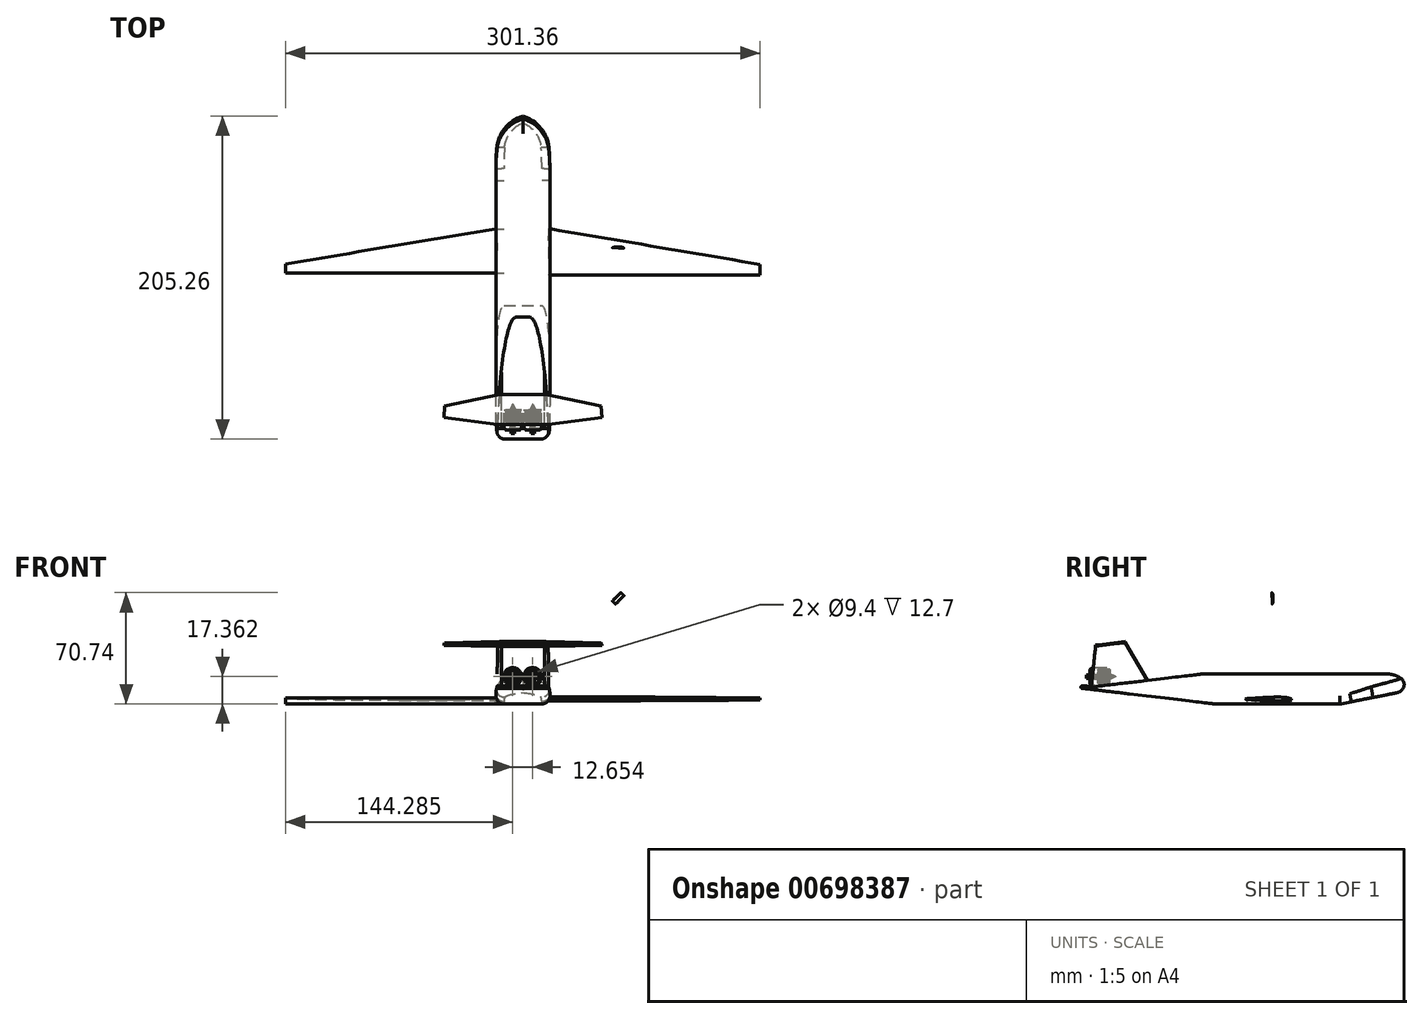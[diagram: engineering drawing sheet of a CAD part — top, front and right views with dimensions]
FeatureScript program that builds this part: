
annotation { "Feature Type Name" : "Feature", "Feature Type Description" : "" }
export const myFeature = defineFeature(function(context is Context, id is Id, definition is map)
    precondition{}
    {
        {
            var Q0;
            Q0=qCreatedBy(makeId("Top.planeOp"),FACE);
            var sketch = newSketch(context, id + "F0", { "sketchPlane" : qUnion([Q0])});
            skLineSegment(sketch, "E0.bottom", {"start": v(17.15, 104.78) * mm, "end": v(-17.14, 104.78) * mm});
            skLineSegment(sketch, "E0.top", {"start": v(17.14, -104.78) * mm, "end": v(-17.15, -104.78) * mm});
            skLineSegment(sketch, "E0.left", {"start": v(17.15, 104.78) * mm, "end": v(17.14, -104.78) * mm});
            skLineSegment(sketch, "E0.right", {"start": v(-17.14, 104.78) * mm, "end": v(-17.15, -104.78) * mm});
            skPoint(sketch, "E0.middle", {"position": v(0, 0) * mm});
            skSolve(sketch);
        }
        {
            var Q0;
            Q0=makeQuery(id+"F0.imprint","IMPRINT",FACE,{"disambiguationData":[TD([[makeQuery(id+"F0.imprint","IMPRINT",EDGE,{"derivedFrom":sQuery(id+"F0.wireOp",EDGE,"E0.bottom")}),1.0]])]});
            extrude(context, id + "F1", {"entities" : qUnion([Q0]), "depth" : 19.05 * mm, "offsetDistance" : 25.4 * mm});
        }
        {
            var Q0;
            Q0=makeQuery(id+"F1.opExtrude","SWEPT_EDGE",EDGE,{"disambiguationData":[OSD([sQuery(id+"F0.wireOp",EDGE,"E0.bottom"),sQuery(id+"F0.wireOp",EDGE,"E0.left")])]});
            var Q1;
            Q1=makeQuery(id+"F1.opExtrude","SWEPT_EDGE",EDGE,{"disambiguationData":[OSD([sQuery(id+"F0.wireOp",EDGE,"E0.bottom"),sQuery(id+"F0.wireOp",EDGE,"E0.right")])]});
            fillet(context, id + "F2", {"entities" : qUnion([Q0, Q1]), "radius" : 25.4 * mm, "tangentPropagation" : true, "allowEdgeOverflow" : false});
        }
        {
            var Q0;
            Q0=makeQuery(id+"F1.opExtrude","SWEPT_FACE",FACE,{"disambiguationData":[OSD([sQuery(id+"F0.wireOp",EDGE,"E0.right")])]});
            var sketch = newSketch(context, id + "F3", { "sketchPlane" : qUnion([Q0])});
            skLineSegment(sketch, "E1.bottom", {"start": v(-28.56, 19.05) * mm, "end": v(-0.6, 19.05) * mm});
            skLineSegment(sketch, "E1.top", {"start": v(-28.56, 0) * mm, "end": v(-0.6, 0) * mm});
            skLineSegment(sketch, "E1.left", {"start": v(-28.56, 19.05) * mm, "end": v(-28.56, 0) * mm});
            skLineSegment(sketch, "E1.right", {"start": v(-0.6, 19.05) * mm, "end": v(-0.6, 0) * mm});
            skLineSegment(sketch, "E2", {"start": v(-28.56, 6.35) * mm, "end": v(-0.6, 6.35) * mm});
            skFitSpline(sketch, "E3", {"points": [v(0.31, 4.07) * mm, v(-28.37, 4.63) * mm, v(-27.2, 2.97) * mm, v(-7.39, 2.92) * mm, v(-5.4, 3.55) * mm, v(0.31, 4.07) * mm]});
            skPoint(sketch, "E4", {"position": v(1.95, 0.65) * mm});
            skPoint(sketch, "E5", {"position": v(4.62, -0.4) * mm});
            skSolve(sketch);
        }
        {
            var Q0;
            Q0=makeQuery(id+"F1.opExtrude","SWEPT_FACE",FACE,{"disambiguationData":[OSD([sQuery(id+"F0.wireOp",EDGE,"E0.left")])]});
            var sketch = newSketch(context, id + "F4", { "sketchPlane" : qUnion([Q0])});
            skLineSegment(sketch, "E6.bottom", {"start": v(-0.54, 19.05) * mm, "end": v(28.71, 19.05) * mm});
            skLineSegment(sketch, "E6.top", {"start": v(-0.54, 0) * mm, "end": v(28.71, 0) * mm});
            skLineSegment(sketch, "E6.left", {"start": v(-0.54, 19.05) * mm, "end": v(-0.54, 0) * mm});
            skLineSegment(sketch, "E6.right", {"start": v(28.71, 19.05) * mm, "end": v(28.71, 0) * mm});
            skLineSegment(sketch, "E7", {"start": v(-0.54, 6.35) * mm, "end": v(28.71, 6.35) * mm});
            skSolve(sketch);
        }
        {
            var Q0;
            {var subQ0=sQuery(id+"F0.wireOp",EDGE,"E0.right");Q0=makeQuery(id+"FtCAVRDJn0QG3nM_1.boolean.opBoolean","SPLIT",EDGE,{"disambiguationData":[TD([makeQuery(id+"FtCAVRDJn0QG3nM_1.opExtrude","SWEPT_FACE",FACE,{"disambiguationData":[OSD([sQuery(id+"F3.wireOp",EDGE,"E1.right")])]})])],"derivedFrom":makeQuery(id+"F1.opExtrude","CAP_EDGE",EDGE,{"disambiguationData":[OSD([subQ0])],"isStart":false})});}
            var Q1;
            {var subQ0=sQuery(id+"F0.wireOp",EDGE,"E0.left");Q1=makeQuery(id+"FXmawxG26BbFG8q_1.boolean.opBoolean","SPLIT",EDGE,{"disambiguationData":[TD([makeQuery(id+"FXmawxG26BbFG8q_1.opExtrude","SWEPT_FACE",FACE,{"disambiguationData":[OSD([sQuery(id+"F4.wireOp",EDGE,"E6.right")])]})])],"derivedFrom":makeQuery(id+"F1.opExtrude","CAP_EDGE",EDGE,{"disambiguationData":[OSD([subQ0])],"isStart":false})});}
            var Q2;
            {var subQ0=sQuery(id+"F0.wireOp",EDGE,"E0.right");Q2=makeQuery(id+"FtCAVRDJn0QG3nM_1.boolean.opBoolean","SPLIT",EDGE,{"disambiguationData":[TD([makeQuery(id+"FtCAVRDJn0QG3nM_1.opExtrude","SWEPT_FACE",FACE,{"disambiguationData":[OSD([sQuery(id+"F3.wireOp",EDGE,"E1.left")])]})])],"derivedFrom":makeQuery(id+"F1.opExtrude","CAP_EDGE",EDGE,{"disambiguationData":[OSD([subQ0])],"isStart":false})});}
            fillet(context, id + "F5", {"entities" : qUnion([Q0, Q1, Q2]), "radius" : 12.7 * mm, "tangentPropagation" : true, "allowEdgeOverflow" : false});
        }
        {
            var Q0;
            {var subQ0=sQuery(id+"F0.wireOp",EDGE,"E0.left");Q0=makeQuery(id+"FXmawxG26BbFG8q_1.boolean.opBoolean","SPLIT",EDGE,{"disambiguationData":[TD([makeQuery(id+"FXmawxG26BbFG8q_1.opExtrude","SWEPT_FACE",FACE,{"disambiguationData":[OSD([sQuery(id+"F4.wireOp",EDGE,"E6.left")])]})])],"derivedFrom":makeQuery(id+"F1.opExtrude","CAP_EDGE",EDGE,{"disambiguationData":[OSD([subQ0])],"isStart":true})});}
            var Q1;
            {var subQ0=sQuery(id+"F0.wireOp",EDGE,"E0.left");Q1=makeQuery(id+"FXmawxG26BbFG8q_1.boolean.opBoolean","SPLIT",EDGE,{"disambiguationData":[TD([makeQuery(id+"FXmawxG26BbFG8q_1.opExtrude","SWEPT_FACE",FACE,{"disambiguationData":[OSD([sQuery(id+"F4.wireOp",EDGE,"E6.right")])]})])],"derivedFrom":makeQuery(id+"F1.opExtrude","CAP_EDGE",EDGE,{"disambiguationData":[OSD([subQ0])],"isStart":true})});}
            var Q2;
            {var subQ0=sQuery(id+"F0.wireOp",EDGE,"E0.right");Q2=makeQuery(id+"FtCAVRDJn0QG3nM_1.boolean.opBoolean","SPLIT",EDGE,{"disambiguationData":[TD([makeQuery(id+"FtCAVRDJn0QG3nM_1.opExtrude","SWEPT_FACE",FACE,{"disambiguationData":[OSD([sQuery(id+"F3.wireOp",EDGE,"E1.left")])]})])],"derivedFrom":makeQuery(id+"F1.opExtrude","CAP_EDGE",EDGE,{"disambiguationData":[OSD([subQ0])],"isStart":true})});}
            fillet(context, id + "F6", {"entities" : qUnion([Q0, Q1, Q2]), "radius" : 5.08 * mm, "tangentPropagation" : true, "allowEdgeOverflow" : false});
        }
        {
            var Q0;
            {var subQ0=sQuery(id+"F4.wireOp",EDGE,"E6.top");Q0=makeQuery(id+"F4.imprint","IMPRINT",FACE,{"disambiguationData":[TD([[makeQuery(id+"F4.imprint","IMPRINT",EDGE,{"derivedFrom":subQ0}),-1.0]])]});}
            var sketch = newSketch(context, id + "F7", { "sketchPlane" : qUnion([Q0])});
            skFitSpline(sketch, "E8", {"points": [v(-0.34, 3.05) * mm, v(29.07, 2.53) * mm, v(26.42, 3.88) * mm, v(4.03, 3.53) * mm, v(-0.34, 3.05) * mm]});
            skPoint(sketch, "E9", {"position": v(24.34, 2.06) * mm});
            skPoint(sketch, "E10", {"position": v(2.71, 2.74) * mm});
            skPoint(sketch, "E11", {"position": v(2.15, 3.42) * mm});
            skPoint(sketch, "E12", {"position": v(1.26, 2.86) * mm});
            skSolve(sketch);
        }
        {
            var Q0;
            Q0=makeQuery(id+"F7.imprint","IMPRINT",FACE,{"disambiguationData":[TD([[makeQuery(id+"F7.imprint","IMPRINT",EDGE,{"derivedFrom":sQuery(id+"F7.wireOp",EDGE,"E8")}),1.0]])]});
            extrude(context, id + "F8", {"entities" : qUnion([Q0]), "operationType" : NewBodyOperationType.ADD, "depth" : 133.54 * mm, "offsetDistance" : 25.4 * mm, "hasSecondDirection" : true, "secondDirectionOppositeDirection" : true, "secondDirectionDepth" : 25.4 * mm});
        }
        {
            var Q0;
            {var subQ0=sQuery(id+"F3.wireOp",EDGE,"E3");var subQ1=sQuery(id+"F3.wireOp",EDGE,"E1.left");var subQ2=makeQuery(id+"F3.imprint","INTERSECT",VERTEX,{"disambiguationData":[OD(0.0)],"derivedFrom":[subQ1,subQ0]});Q0=makeQuery(id+"F3.imprint","IMPRINT",FACE,{"disambiguationData":[TD([[makeQuery(id+"F3.imprint","IMPRINT",EDGE,{"disambiguationData":[TD([[subQ2,-1.0]])],"derivedFrom":subQ1}),1.0]])]});}
            extrude(context, id + "F9", {"entities" : qUnion([Q0]), "operationType" : NewBodyOperationType.ADD, "depth" : 133.54 * mm, "offsetDistance" : 25.4 * mm, "hasSecondDirection" : true, "secondDirectionOppositeDirection" : true, "secondDirectionDepth" : 25.4 * mm});
        }
        {
            var Q0;
            Q0=qCreatedBy(makeId("Right.planeOp"),FACE);
            var sketch = newSketch(context, id + "F10", { "sketchPlane" : qUnion([Q0])});
            skLineSegment(sketch, "E13.bottom", {"start": v(19.48, 67.25) * mm, "end": v(46.84, 67.25) * mm});
            skLineSegment(sketch, "E13.top", {"start": v(19.48, 55.36) * mm, "end": v(46.84, 55.36) * mm});
            skLineSegment(sketch, "E13.left", {"start": v(19.48, 67.25) * mm, "end": v(19.48, 55.36) * mm});
            skLineSegment(sketch, "E13.right", {"start": v(46.84, 67.25) * mm, "end": v(46.84, 55.36) * mm});
            skSolve(sketch);
        }
        {
            var Q0;
            Q0=makeQuery(id+"F10.imprint","IMPRINT",FACE,{"disambiguationData":[TD([[makeQuery(id+"F10.imprint","IMPRINT",EDGE,{"derivedFrom":sQuery(id+"F10.wireOp",EDGE,"E13.bottom")}),-1.0]])]});
            extrude(context, id + "F11", {"entities" : qUnion([Q0]), "depth" : 81.28 * mm, "offsetDistance" : 25.4 * mm});
        }
        {
            var Q0;
            Q0=makeQuery(id+"F11.opExtrude","SWEPT_FACE",FACE,{"disambiguationData":[OSD([sQuery(id+"F10.wireOp",EDGE,"E13.bottom")])]});
            var sketch = newSketch(context, id + "F12", { "sketchPlane" : qUnion([Q0])});
            skLineSegment(sketch, "E14", {"start": v(0, 46.84) * mm, "end": v(81.28, 27.08) * mm});
            skSolve(sketch);
        }
        {
            var Q0;
            {var subQ0=sQuery(id+"F12.wireOp",EDGE,"E14");Q0=makeQuery(id+"F12.imprint","IMPRINT",FACE,{"disambiguationData":[TD([[makeQuery(id+"F12.imprint","IMPRINT",EDGE,{"derivedFrom":subQ0}),1.0]])]});}
            extrude(context, id + "F13", {"entities" : qUnion([Q0]), "operationType" : NewBodyOperationType.REMOVE, "oppositeDirection" : true, "depth" : 25.4 * mm, "offsetDistance" : 25.4 * mm});
        }
        {
            var Q0;
            Q0=makeQuery(id+"F11.opExtrude","SWEPT_BODY",BODY,{"disambiguationData":[OSD([sQuery(id+"F10.wireOp",EDGE,"E13.bottom"),sQuery(id+"F10.wireOp",EDGE,"E13.top"),sQuery(id+"F10.wireOp",EDGE,"E13.left"),sQuery(id+"F10.wireOp",EDGE,"E13.right")])]});
            deleteBodies(context, id + "F14", {"entities" : qUnion([Q0])});
        }
        {
            var Q0;
            {var subQ0=sQuery(id+"F4.wireOp",EDGE,"E6.top");Q0=makeQuery(id+"F4.imprint","IMPRINT",FACE,{"disambiguationData":[TD([[makeQuery(id+"F4.imprint","IMPRINT",EDGE,{"derivedFrom":subQ0}),-1.0]])]});}
            var sketch = newSketch(context, id + "F15", { "sketchPlane" : qUnion([Q0])});
            skLineSegment(sketch, "E15.bottom", {"start": v(0, 5.25) * mm, "end": v(28.83, 5.25) * mm});
            skLineSegment(sketch, "E15.top", {"start": v(0, 4.61) * mm, "end": v(28.83, 4.61) * mm});
            skLineSegment(sketch, "E15.left", {"start": v(0, 5.25) * mm, "end": v(0, 4.61) * mm});
            skLineSegment(sketch, "E15.right", {"start": v(28.83, 5.25) * mm, "end": v(28.83, 4.61) * mm});
            skSolve(sketch);
        }
        {
            var Q0;
            {var subQ0=sQuery(id+"F15.wireOp",EDGE,"E15.left");Q0=makeQuery(id+"F15.imprint","IMPRINT",FACE,{"disambiguationData":[TD([[makeQuery(id+"F15.imprint","IMPRINT",EDGE,{"derivedFrom":subQ0}),1.0]])]});}
            extrude(context, id + "F16", {"entities" : qUnion([Q0]), "operationType" : NewBodyOperationType.ADD, "depth" : 133.54 * mm, "offsetDistance" : 25.4 * mm});
        }
        {
            var Q0;
            Q0=makeQuery(id+"F16.opExtrude","SWEPT_FACE",FACE,{"disambiguationData":[OSD([sQuery(id+"F15.wireOp",EDGE,"E15.bottom")])]});
            var sketch = newSketch(context, id + "F17", { "sketchPlane" : qUnion([Q0])});
            skLineSegment(sketch, "E16", {"start": v(17.15, 28.71) * mm, "end": v(150.68, 6.07) * mm});
            skSolve(sketch);
        }
        {
            var Q0;
            {var subQ0=sQuery(id+"F17.wireOp",EDGE,"E16");Q0=makeQuery(id+"F17.imprint","IMPRINT",FACE,{"disambiguationData":[TD([[makeQuery(id+"F17.imprint","IMPRINT",EDGE,{"derivedFrom":subQ0}),1.0]])]});}
            extrude(context, id + "F18", {"entities" : qUnion([Q0]), "operationType" : NewBodyOperationType.REMOVE, "oppositeDirection" : true, "depth" : 25.4 * mm, "offsetDistance" : 25.4 * mm});
        }
        {
            var Q0;
            Q0=makeQuery(id+"F16.opExtrude","SWEPT_FACE",FACE,{"disambiguationData":[OSD([sQuery(id+"F15.wireOp",EDGE,"E15.bottom")])]});
            var sketch = newSketch(context, id + "F19", { "sketchPlane" : qUnion([Q0])});
            skLineSegment(sketch, "E17", {"start": v(17.15, 28.71) * mm, "end": v(150.68, 6.07) * mm});
            skLineSegment(sketch, "E18", {"start": v(150.68, 6.07) * mm, "end": v(150.68, 0) * mm});
            skLineSegment(sketch, "E19", {"start": v(150.68, 0) * mm, "end": v(17.14, 0) * mm});
            skLineSegment(sketch, "E20", {"start": v(17.14, 0) * mm, "end": v(17.15, 28.71) * mm});
            skSolve(sketch);
        }
        {
            var Q0;
            Q0=makeQuery(id+"F19.imprint","IMPRINT",FACE,{"disambiguationData":[TD([[makeQuery(id+"F19.imprint","IMPRINT",EDGE,{"derivedFrom":sQuery(id+"F19.wireOp",EDGE,"E17")}),-1.0]])]});
            extrude(context, id + "F20", {"entities" : qUnion([Q0]), "operationType" : NewBodyOperationType.REMOVE, "endBound" : BoundingType.UP_TO_NEXT, "oppositeDirection" : true, "depth" : 2.54 * mm, "offsetDistance" : 25.4 * mm});
        }
        {
            var Q0;
            Q0=makeQuery(id+"F1.opExtrude","SWEPT_FACE",FACE,{"disambiguationData":[OSD([sQuery(id+"F0.wireOp",EDGE,"E0.right")])]});
            var sketch = newSketch(context, id + "F21", { "sketchPlane" : qUnion([Q0])});
            skLineSegment(sketch, "E21.bottom", {"start": v(-28.66, 6.35) * mm, "end": v(-0.3, 6.35) * mm});
            skLineSegment(sketch, "E21.top", {"start": v(-28.66, 5.62) * mm, "end": v(-0.3, 5.62) * mm});
            skLineSegment(sketch, "E21.left", {"start": v(-28.66, 6.35) * mm, "end": v(-28.66, 5.62) * mm});
            skLineSegment(sketch, "E21.right", {"start": v(-0.3, 6.35) * mm, "end": v(-0.3, 5.62) * mm});
            skSolve(sketch);
        }
        {
            var Q0;
            Q0=makeQuery(id+"F21.imprint","IMPRINT",FACE,{"disambiguationData":[TD([[makeQuery(id+"F21.imprint","IMPRINT",EDGE,{"derivedFrom":sQuery(id+"F21.wireOp",EDGE,"E21.bottom")}),1.0]])]});
            extrude(context, id + "F22", {"entities" : qUnion([Q0]), "operationType" : NewBodyOperationType.ADD, "depth" : 133.54 * mm, "offsetDistance" : 25.4 * mm});
        }
        {
            var Q0;
            Q0=makeQuery(id+"F22.opExtrude","SWEPT_FACE",FACE,{"disambiguationData":[OSD([sQuery(id+"F21.wireOp",EDGE,"E21.bottom")])]});
            var sketch = newSketch(context, id + "F23", { "sketchPlane" : qUnion([Q0])});
            skLineSegment(sketch, "E22", {"start": v(-17.14, 28.66) * mm, "end": v(-150.68, 6.36) * mm});
            skSolve(sketch);
        }
        {
            var Q0;
            {var subQ0=sQuery(id+"F23.wireOp",EDGE,"E22");Q0=makeQuery(id+"F23.imprint","IMPRINT",FACE,{"disambiguationData":[TD([[makeQuery(id+"F23.imprint","IMPRINT",EDGE,{"derivedFrom":subQ0}),-1.0]])]});}
            extrude(context, id + "F24", {"entities" : qUnion([Q0]), "operationType" : NewBodyOperationType.REMOVE, "oppositeDirection" : true, "depth" : 25.4 * mm, "offsetDistance" : 25.4 * mm});
        }
        {
            var Q0;
            Q0=makeQuery(id+"F22.opExtrude","SWEPT_FACE",FACE,{"disambiguationData":[OSD([sQuery(id+"F21.wireOp",EDGE,"E21.bottom")])]});
            extrude(context, id + "F25", {"entities" : qUnion([Q0]), "operationType" : NewBodyOperationType.REMOVE, "endBound" : BoundingType.UP_TO_NEXT, "oppositeDirection" : true, "depth" : 25.4 * mm, "offsetDistance" : 25.4 * mm});
        }
        {
            var Q0;
            Q0=makeQuery(id+"F5.opFillet","BLEND_EDGE",EDGE,{"blendedFrom":[makeQuery(id+"F1.opExtrude","CAP_EDGE",EDGE,{"disambiguationData":[OSD([sQuery(id+"F0.wireOp",EDGE,"E0.left")])],"isStart":false}),makeQuery(id+"F1.opExtrude","SWEPT_FACE",FACE,{"disambiguationData":[OSD([sQuery(id+"F0.wireOp",EDGE,"E0.top")])]})],"blendedInto":[makeQuery(id+"F1.opExtrude","SWEPT_FACE",FACE,{"disambiguationData":[OSD([sQuery(id+"F0.wireOp",EDGE,"E0.top")])]})]});
            fillet(context, id + "F26", {"entities" : qUnion([Q0]), "radius" : 5.08 * mm, "tangentPropagation" : true, "allowEdgeOverflow" : false});
        }
        {
            var Q0;
            {var subQ0=sQuery(id+"F0.wireOp",EDGE,"E0.left");var subQ2=makeQuery(id+"F1.opExtrude","SWEPT_EDGE",EDGE,{"disambiguationData":[OSD([sQuery(id+"F0.wireOp",EDGE,"E0.top"),subQ0])]});Q0=makeQuery(id+"F4.imprint","IMPRINT",FACE,{"disambiguationData":[TD([[makeQuery(id+"F4.imprint","IMPRINT",EDGE,{"derivedFrom":subQ2}),1.0]])]});}
            var sketch = newSketch(context, id + "F27", { "sketchPlane" : qUnion([Q0])});
            skLineSegment(sketch, "E23", {"start": v(-12.6, 20.8) * mm, "end": v(-104.7, 9.97) * mm});
            skLineSegment(sketch, "E24", {"start": v(-104.7, 9.97) * mm, "end": v(-20.12, 0) * mm});
            skLineSegment(sketch, "E25", {"start": v(-12.6, 20.8) * mm, "end": v(-20.12, 0) * mm});
            skSolve(sketch);
        }
        {
            var Q0;
            {var subQ6=sQuery(id+"F27.wireOp",EDGE,"E24");Q0=makeQuery(id+"F27.imprint","IMPRINT",FACE,{"disambiguationData":[TD([[makeQuery(id+"F27.imprint","IMPRINT",EDGE,{"derivedFrom":subQ6}),-1.0]])]});}
            extrude(context, id + "F28", {"entities" : qUnion([Q0]), "operationType" : NewBodyOperationType.REMOVE, "endBound" : BoundingType.THROUGH_ALL, "oppositeDirection" : true, "depth" : 25.4 * mm, "offsetDistance" : 25.4 * mm});
        }
        {
            var Q0;
            Q0=makeQuery(id+"F28.boolean.opBoolean","COPY",FACE,{"derivedFrom":makeQuery(id+"F28.opExtrude","SWEPT_FACE",FACE,{"disambiguationData":[OSD([sQuery(id+"F27.wireOp",EDGE,"E23")])]})});
            var sketch = newSketch(context, id + "F29", { "sketchPlane" : qUnion([Q0])});
            skLineSegment(sketch, "E26", {"start": v(-12.1, -102.82) * mm, "end": v(12.1, -102.82) * mm});
            skLineSegment(sketch, "E27", {"start": v(12.1, -102.82) * mm, "end": v(12.1, -96.37) * mm});
            skLineSegment(sketch, "E28", {"start": v(12.1, -96.37) * mm, "end": v(-12.1, -96.37) * mm});
            skLineSegment(sketch, "E29", {"start": v(-12.1, -96.37) * mm, "end": v(-12.1, -102.82) * mm});
            skLineSegment(sketch, "E30", {"start": v(12.1, -96.37) * mm, "end": v(16.37, -96.37) * mm});
            skLineSegment(sketch, "E31", {"start": v(16.37, -96.37) * mm, "end": v(16.43, -97.78) * mm});
            skLineSegment(sketch, "E32", {"start": v(16.43, -97.78) * mm, "end": v(12.1, -102.82) * mm});
            skLineSegment(sketch, "E33", {"start": v(-12.1, -102.82) * mm, "end": v(-16.43, -97.78) * mm});
            skLineSegment(sketch, "E34", {"start": v(-12.1, -96.37) * mm, "end": v(-16.37, -96.37) * mm});
            skSolve(sketch);
        }
        {
            var Q0;
            Q0=makeQuery(id+"F29.imprint","IMPRINT",FACE,{"disambiguationData":[TD([[makeQuery(id+"F29.imprint","IMPRINT",EDGE,{"derivedFrom":sQuery(id+"F29.wireOp",EDGE,"E26")}),1.0]])]});
            var Q1;
            Q1=makeQuery(id+"F29.imprint","IMPRINT",FACE,{"disambiguationData":[TD([[makeQuery(id+"F29.imprint","IMPRINT",EDGE,{"derivedFrom":sQuery(id+"F29.wireOp",EDGE,"E27")}),-1.0]])]});
            var Q2;
            Q2=makeQuery(id+"F29.imprint","IMPRINT",FACE,{"disambiguationData":[TD([[makeQuery(id+"F29.imprint","IMPRINT",EDGE,{"derivedFrom":sQuery(id+"F29.wireOp",EDGE,"E29")}),-1.0]])]});
            var Q3;
            Q3=makeQuery(id+"F29.imprint","IMPRINT",FACE,{"disambiguationData":[TD([[makeQuery(id+"F29.imprint","IMPRINT",EDGE,{"derivedFrom":sQuery(id+"F29.wireOp",EDGE,"E32")}),1.0]])]});
            var Q4;
            Q4=makeQuery(id+"F29.imprint","IMPRINT",FACE,{"disambiguationData":[TD([[makeQuery(id+"F29.imprint","IMPRINT",EDGE,{"derivedFrom":sQuery(id+"F29.wireOp",EDGE,"E33")}),1.0]])]});
            extrude(context, id + "F30", {"entities" : qUnion([Q0, Q1, Q2, Q3, Q4]), "operationType" : NewBodyOperationType.ADD, "depth" : 1.27 * mm, "offsetDistance" : 25.4 * mm});
        }
        {
            var Q0;
            Q0=makeQuery(id+"F30.opExtrude","CAP_EDGE",EDGE,{"disambiguationData":[OSD([sQuery(id+"F29.wireOp",EDGE,"E28"),sQuery(id+"F29.wireOp",EDGE,"E30"),sQuery(id+"F29.wireOp",EDGE,"E34")])],"isStart":false});
            fillet(context, id + "F31", {"entities" : qUnion([Q0]), "radius" : 15.94 * mm, "tangentPropagation" : true, "allowEdgeOverflow" : false});
        }
        {
            var Q0;
            Q0=qCreatedBy(makeId("Right.planeOp"),FACE);
            var sketch = newSketch(context, id + "F32", { "sketchPlane" : qUnion([Q0])});
            skLineSegment(sketch, "E35", {"start": v(103.83, 8.7) * mm, "end": v(59.96, 0) * mm});
            skLineSegment(sketch, "E36", {"start": v(103.83, 8.7) * mm, "end": v(106.15, -3) * mm});
            skLineSegment(sketch, "E37", {"start": v(106.15, -3) * mm, "end": v(61.39, -8.19) * mm});
            skLineSegment(sketch, "E38", {"start": v(61.39, -8.19) * mm, "end": v(59.96, 0) * mm});
            skSolve(sketch);
        }
        {
            var Q0;
            Q0=makeQuery(id+"F32.imprint","IMPRINT",FACE,{"disambiguationData":[TD([[makeQuery(id+"F32.imprint","IMPRINT",EDGE,{"derivedFrom":sQuery(id+"F32.wireOp",EDGE,"E35")}),1.0]])]});
            extrude(context, id + "F33", {"entities" : qUnion([Q0]), "operationType" : NewBodyOperationType.REMOVE, "endBound" : BoundingType.SYMMETRIC, "oppositeDirection" : true, "depth" : 77.22 * mm, "offsetDistance" : 25.4 * mm});
        }
        {
            var Q0;
            {var subQ0=sQuery(id+"F0.wireOp",EDGE,"E0.right");var subQ1=sQuery(id+"F0.wireOp",EDGE,"E0.left");var subQ2=sQuery(id+"F0.wireOp",EDGE,"E0.top");var subQ3=sQuery(id+"F0.wireOp",EDGE,"E0.bottom");Q0=makeQuery(id+"F33.boolean.opBoolean","INTERSECT",EDGE,{"derivedFrom":[makeQuery(id+"F6.opFillet","BLEND_FACE",FACE,{"disambiguationData":[OSD([subQ3,subQ2,subQ1,subQ0]),TDD([makeQuery(id+"F2.opFillet","BLEND_EDGE",EDGE,{"blendedFrom":[makeQuery(id+"F1.opExtrude","SWEPT_EDGE",EDGE,{"disambiguationData":[OSD([subQ3,subQ0])]}),makeQuery(id+"F1.opExtrude","CAP_FACE",FACE,{"disambiguationData":[OSD([subQ3,subQ2,subQ1,subQ0])],"isStart":true})],"blendedInto":[makeQuery(id+"F1.opExtrude","CAP_FACE",FACE,{"disambiguationData":[OSD([subQ3,subQ2,subQ1,subQ0])],"isStart":true})]})])]}),makeQuery(id+"F33.opExtrude","SWEPT_FACE",FACE,{"disambiguationData":[OSD([sQuery(id+"F32.wireOp",EDGE,"E35")])]})]});}
            var Q1;
            Q1=makeQuery(id+"F33.boolean.opBoolean","INTERSECT",EDGE,{"derivedFrom":[makeQuery(id+"F6.opFillet","BLEND_FACE",FACE,{"disambiguationData":[OSD([sQuery(id+"F0.wireOp",EDGE,"E0.right")])]}),makeQuery(id+"F33.opExtrude","SWEPT_FACE",FACE,{"disambiguationData":[OSD([sQuery(id+"F32.wireOp",EDGE,"E35")])]})]});
            var Q2;
            Q2=makeQuery(id+"F33.boolean.opBoolean","COPY",FACE,{"derivedFrom":makeQuery(id+"F33.opExtrude","SWEPT_FACE",FACE,{"disambiguationData":[OSD([sQuery(id+"F32.wireOp",EDGE,"E35")])]})});
            fillet(context, id + "F34", {"entities" : qUnion([Q0, Q1, Q2]), "radius" : 5.08 * mm, "tangentPropagation" : true, "allowEdgeOverflow" : false});
        }
        {
            var Q0;
            Q0=makeQuery(id+"F28.boolean.opBoolean","COPY",FACE,{"derivedFrom":makeQuery(id+"F28.opExtrude","SWEPT_FACE",FACE,{"disambiguationData":[OSD([sQuery(id+"F27.wireOp",EDGE,"E23")])]})});
            var sketch = newSketch(context, id + "F35", { "sketchPlane" : qUnion([Q0])});
            skLineSegment(sketch, "E39.bottom", {"start": v(-16.37, -96.37) * mm, "end": v(-13.63, -96.37) * mm});
            skLineSegment(sketch, "E39.top", {"start": v(-16.37, -60.4) * mm, "end": v(-13.63, -60.4) * mm});
            skLineSegment(sketch, "E39.left", {"start": v(-16.37, -96.37) * mm, "end": v(-16.37, -60.4) * mm});
            skLineSegment(sketch, "E39.right", {"start": v(-13.63, -96.37) * mm, "end": v(-13.63, -60.4) * mm});
            skLineSegment(sketch, "E40.bottom", {"start": v(16.37, -96.37) * mm, "end": v(13.81, -96.37) * mm});
            skLineSegment(sketch, "E40.top", {"start": v(16.37, -60.4) * mm, "end": v(13.81, -60.4) * mm});
            skLineSegment(sketch, "E40.left", {"start": v(16.37, -96.37) * mm, "end": v(16.37, -60.4) * mm});
            skLineSegment(sketch, "E40.right", {"start": v(13.81, -96.37) * mm, "end": v(13.81, -60.4) * mm});
            skSolve(sketch);
        }
        {
            var Q0;
            {var subQ0=sQuery(id+"F35.wireOp",EDGE,"E39.bottom");Q0=makeQuery(id+"F35.imprint","IMPRINT",FACE,{"disambiguationData":[TD([[makeQuery(id+"F35.imprint","IMPRINT",EDGE,{"derivedFrom":subQ0}),-1.0]])]});}
            var Q1;
            {var subQ0=sQuery(id+"F35.wireOp",EDGE,"E40.bottom");Q1=makeQuery(id+"F35.imprint","IMPRINT",FACE,{"disambiguationData":[TD([[makeQuery(id+"F35.imprint","IMPRINT",EDGE,{"derivedFrom":subQ0}),-1.0]])]});}
            extrude(context, id + "F36", {"entities" : qUnion([Q0, Q1]), "operationType" : NewBodyOperationType.ADD, "depth" : 25.4 * mm, "offsetDistance" : 25.4 * mm});
        }
        {
            var Q0;
            Q0=makeQuery(id+"F36.opExtrude","SWEPT_FACE",FACE,{"disambiguationData":[OSD([sQuery(id+"F35.wireOp",EDGE,"E39.right")])]});
            var sketch = newSketch(context, id + "F37", { "sketchPlane" : qUnion([Q0])});
            skLineSegment(sketch, "E41", {"start": v(-98.3, 10.73) * mm, "end": v(-95.57, 36.62) * mm});
            skLineSegment(sketch, "E42", {"start": v(-76.52, 38.86) * mm, "end": v(-62.57, 14.93) * mm});
            skSolve(sketch);
        }
        {
            var Q0;
            {var subQ0=sQuery(id+"F37.wireOp",EDGE,"qg9zDmBJ-7vhe-sEv8-FbPa-SV9eqWlspidy");Q0=makeQuery(id+"F37.imprint","IMPRINT",FACE,{"disambiguationData":[TD([[makeQuery(id+"F37.imprint","IMPRINT",EDGE,{"derivedFrom":subQ0}),1.0]])]});}
            var Q1;
            {var subQ0=sQuery(id+"F37.wireOp",EDGE,"E41");Q1=makeQuery(id+"F37.imprint","IMPRINT",FACE,{"disambiguationData":[TD([[makeQuery(id+"F37.imprint","IMPRINT",EDGE,{"derivedFrom":subQ0}),1.0]])]});}
            var Q2;
            {var subQ0=sQuery(id+"F37.wireOp",EDGE,"E42");Q2=makeQuery(id+"F37.imprint","IMPRINT",FACE,{"disambiguationData":[TD([[makeQuery(id+"F37.imprint","IMPRINT",EDGE,{"derivedFrom":subQ0}),1.0]])]});}
            extrude(context, id + "F38", {"entities" : qUnion([Q0, Q1, Q2]), "operationType" : NewBodyOperationType.REMOVE, "oppositeDirection" : true, "depth" : 25.4 * mm, "offsetDistance" : 25.4 * mm});
        }
        {
            var Q0;
            Q0=makeQuery(id+"F36.opExtrude","SWEPT_FACE",FACE,{"disambiguationData":[OSD([sQuery(id+"F35.wireOp",EDGE,"E40.right")])]});
            var sketch = newSketch(context, id + "F39", { "sketchPlane" : qUnion([Q0])});
            skLineSegment(sketch, "E43", {"start": v(98.3, 10.73) * mm, "end": v(95.57, 36.62) * mm});
            skLineSegment(sketch, "E44", {"start": v(62.57, 14.93) * mm, "end": v(76.52, 38.86) * mm});
            skSolve(sketch);
        }
        {
            var Q0;
            {var subQ0=sQuery(id+"F39.wireOp",EDGE,"E44");Q0=makeQuery(id+"F39.imprint","IMPRINT",FACE,{"disambiguationData":[TD([[makeQuery(id+"F39.imprint","IMPRINT",EDGE,{"derivedFrom":subQ0}),1.0]])]});}
            var Q1;
            {var subQ0=sQuery(id+"F39.wireOp",EDGE,"E43");Q1=makeQuery(id+"F39.imprint","IMPRINT",FACE,{"disambiguationData":[TD([[makeQuery(id+"F39.imprint","IMPRINT",EDGE,{"derivedFrom":subQ0}),-1.0]])]});}
            extrude(context, id + "F40", {"entities" : qUnion([Q0, Q1]), "operationType" : NewBodyOperationType.REMOVE, "oppositeDirection" : true, "depth" : 25.4 * mm, "offsetDistance" : 25.4 * mm});
        }
        {
            var Q0;
            Q0=makeQuery(id+"F36.opExtrude","CAP_FACE",FACE,{"disambiguationData":[OSD([sQuery(id+"F0.wireOp",EDGE,"E0.right"),sQuery(id+"F27.wireOp",EDGE,"E23"),sQuery(id+"F35.wireOp",EDGE,"E39.bottom"),sQuery(id+"F35.wireOp",EDGE,"E39.top"),sQuery(id+"F35.wireOp",EDGE,"E39.right")])],"isStart":false});
            var sketch = newSketch(context, id + "F41", { "sketchPlane" : qUnion([Q0])});
            skLineSegment(sketch, "E45.bottom", {"start": v(-16.1, -90.64) * mm, "end": v(16.04, -90.64) * mm});
            skLineSegment(sketch, "E45.left", {"start": v(-16.1, -90.64) * mm, "end": v(-16.1, -71.7) * mm});
            skLineSegment(sketch, "E46", {"start": v(16.04, -90.64) * mm, "end": v(-16.1, -90.64) * mm});
            skLineSegment(sketch, "E47", {"start": v(-16.1, -90.64) * mm, "end": v(-14.85, -71.46) * mm});
            skLineSegment(sketch, "E48", {"start": v(-14.85, -71.46) * mm, "end": v(-13.63, -71.46) * mm});
            skLineSegment(sketch, "E49", {"start": v(-13.63, -71.46) * mm, "end": v(13.82, -71.46) * mm});
            skLineSegment(sketch, "E50", {"start": v(13.82, -71.46) * mm, "end": v(14.83, -71.46) * mm});
            skLineSegment(sketch, "E51", {"start": v(14.83, -71.46) * mm, "end": v(16.04, -90.64) * mm});
            skSolve(sketch);
        }
        {
            var Q0;
            Q0=makeQuery(id+"F41.imprint","IMPRINT",FACE,{"disambiguationData":[TD([[makeQuery(id+"F41.imprint","IMPRINT",EDGE,{"derivedFrom":sQuery(id+"F41.wireOp",EDGE,"E49")}),-1.0]])]});
            var Q1;
            {var subQ2=sQuery(id+"F41.wireOp",EDGE,"E47");Q1=makeQuery(id+"F41.imprint","IMPRINT",FACE,{"disambiguationData":[TD([[makeQuery(id+"F41.imprint","IMPRINT",EDGE,{"derivedFrom":subQ2}),-1.0]])]});}
            extrude(context, id + "F42", {"entities" : qUnion([Q0, Q1]), "operationType" : NewBodyOperationType.ADD, "depth" : 0.76 * mm, "offsetDistance" : 25.4 * mm});
        }
        {
            var Q0;
            Q0=makeQuery(id+"F42.opExtrude","SWEPT_FACE",FACE,{"disambiguationData":[OSD([sQuery(id+"F41.wireOp",EDGE,"E47")])]});
            extrude(context, id + "F43", {"entities" : qUnion([Q0]), "operationType" : NewBodyOperationType.ADD, "depth" : 34.3 * mm, "offsetDistance" : 25.4 * mm});
        }
        {
            var Q0;
            Q0=makeQuery(id+"F42.opExtrude","SWEPT_FACE",FACE,{"disambiguationData":[OSD([sQuery(id+"F41.wireOp",EDGE,"E51")])]});
            var sketch = newSketch(context, id + "F44", { "sketchPlane" : qUnion([Q0])});
            skLineSegment(sketch, "E52", {"start": v(-96.4, 36.5) * mm, "end": v(-96.5, 37.26) * mm});
            skLineSegment(sketch, "E53", {"start": v(-96.5, 37.26) * mm, "end": v(-77.4, 39.5) * mm});
            skLineSegment(sketch, "E54", {"start": v(-77.4, 39.5) * mm, "end": v(-77.32, 38.75) * mm});
            skLineSegment(sketch, "E55", {"start": v(-77.32, 38.75) * mm, "end": v(-96.4, 36.5) * mm});
            skSolve(sketch);
        }
        {
            var Q0;
            Q0=makeQuery(id+"F44.imprint","IMPRINT",FACE,{"disambiguationData":[TD([[makeQuery(id+"F44.imprint","IMPRINT",EDGE,{"derivedFrom":sQuery(id+"F44.wireOp",EDGE,"E52")}),1.0]])]});
            extrude(context, id + "F45", {"entities" : qUnion([Q0]), "operationType" : NewBodyOperationType.ADD, "depth" : 34.3 * mm, "offsetDistance" : 25.4 * mm});
        }
        {
            var Q0;
            {var subQ0=sQuery(id+"F41.wireOp",EDGE,"E47");Q0=makeQuery(id+"F45.boolean.opBoolean","MERGE",FACE,{"derivedFrom":[makeQuery(id+"F43.boolean.opBoolean","MERGE",FACE,{"derivedFrom":[makeQuery(id+"F42.opExtrude","CAP_FACE",FACE,{"disambiguationData":[OSD([sQuery(id+"F41.wireOp",EDGE,"E46"),subQ0,sQuery(id+"F41.wireOp",EDGE,"E48"),sQuery(id+"F41.wireOp",EDGE,"E49"),sQuery(id+"F41.wireOp",EDGE,"E50"),sQuery(id+"F41.wireOp",EDGE,"E51")])],"isStart":false}),makeQuery(id+"F43.opExtrude","SWEPT_FACE",FACE,{"disambiguationData":[OSD([subQ0]),TDD([makeQuery(id+"F42.opExtrude","CAP_EDGE",EDGE,{"disambiguationData":[OSD([subQ0])],"isStart":false})])]})]}),makeQuery(id+"F45.opExtrude","SWEPT_FACE",FACE,{"disambiguationData":[OSD([sQuery(id+"F44.wireOp",EDGE,"E53")])]})]});}
            var sketch = newSketch(context, id + "F46", { "sketchPlane" : qUnion([Q0])});
            skLineSegment(sketch, "E56", {"start": v(-14.85, -71.46) * mm, "end": v(-49.7, -78.82) * mm});
            skLineSegment(sketch, "E57", {"start": v(14.83, -71.46) * mm, "end": v(49.66, -78.88) * mm});
            skSolve(sketch);
        }
        {
            var Q0;
            {var subQ0=sQuery(id+"F46.wireOp",EDGE,"E57");Q0=makeQuery(id+"F46.imprint","IMPRINT",FACE,{"disambiguationData":[TD([[makeQuery(id+"F46.imprint","IMPRINT",EDGE,{"derivedFrom":subQ0}),1.0]])]});}
            var Q1;
            {var subQ0=sQuery(id+"F46.wireOp",EDGE,"E56");Q1=makeQuery(id+"F46.imprint","IMPRINT",FACE,{"disambiguationData":[TD([[makeQuery(id+"F46.imprint","IMPRINT",EDGE,{"derivedFrom":subQ0}),-1.0]])]});}
            extrude(context, id + "F47", {"entities" : qUnion([Q0, Q1]), "operationType" : NewBodyOperationType.REMOVE, "oppositeDirection" : true, "depth" : 0.76 * mm, "offsetDistance" : 25.4 * mm});
        }
        {
            var Q0;
            {var subQ0=sQuery(id+"F41.wireOp",EDGE,"E47");Q0=makeQuery(id+"F45.boolean.opBoolean","MERGE",FACE,{"derivedFrom":[makeQuery(id+"F43.boolean.opBoolean","MERGE",FACE,{"derivedFrom":[makeQuery(id+"F42.opExtrude","CAP_FACE",FACE,{"disambiguationData":[OSD([sQuery(id+"F41.wireOp",EDGE,"E46"),subQ0,sQuery(id+"F41.wireOp",EDGE,"E48"),sQuery(id+"F41.wireOp",EDGE,"E49"),sQuery(id+"F41.wireOp",EDGE,"E50"),sQuery(id+"F41.wireOp",EDGE,"E51")])],"isStart":false}),makeQuery(id+"F43.opExtrude","SWEPT_FACE",FACE,{"disambiguationData":[OSD([subQ0]),TDD([makeQuery(id+"F42.opExtrude","CAP_EDGE",EDGE,{"disambiguationData":[OSD([subQ0])],"isStart":false})])]})]}),makeQuery(id+"F45.opExtrude","SWEPT_FACE",FACE,{"disambiguationData":[OSD([sQuery(id+"F44.wireOp",EDGE,"E53")])]})]});}
            var sketch = newSketch(context, id + "F48", { "sketchPlane" : qUnion([Q0])});
            skLineSegment(sketch, "E58", {"start": v(-16.1, -90.64) * mm, "end": v(-50.17, -86.2) * mm});
            skLineSegment(sketch, "E59", {"start": v(16.04, -90.64) * mm, "end": v(50.12, -86.27) * mm});
            skSolve(sketch);
        }
        {
            var Q0;
            {var subQ0=sQuery(id+"F48.wireOp",EDGE,"E59");Q0=makeQuery(id+"F48.imprint","IMPRINT",FACE,{"disambiguationData":[TD([[makeQuery(id+"F48.imprint","IMPRINT",EDGE,{"derivedFrom":subQ0}),-1.0]])]});}
            var Q1;
            {var subQ0=sQuery(id+"F48.wireOp",EDGE,"E58");Q1=makeQuery(id+"F48.imprint","IMPRINT",FACE,{"disambiguationData":[TD([[makeQuery(id+"F48.imprint","IMPRINT",EDGE,{"derivedFrom":subQ0}),1.0]])]});}
            extrude(context, id + "F49", {"entities" : qUnion([Q0, Q1]), "operationType" : NewBodyOperationType.REMOVE, "oppositeDirection" : true, "depth" : 0.76 * mm, "offsetDistance" : 25.4 * mm});
        }
        {
            var Q0;
            Q0=qCreatedBy(makeId("Front.planeOp"),FACE);
            cPlane(context, id + "F50", {"entities" : qUnion([Q0]), "cplaneType" : CPlaneType.OFFSET, "offset" : 86.36 * mm, "width" : 152.4 * mm, "height" : 152.4 * mm});
        }
        {
            var Q0;
            Q0=qCreatedBy(id+"F50.planeOp",FACE);
            var sketch = newSketch(context, id + "F51", { "sketchPlane" : qUnion([Q0])});
            skCircle(sketch, "E60", {"center": v(-6.4, 17.36) * mm, "radius": 5.72 * mm});
            skCircle(sketch, "E61", {"center": v(6.26, 17.36) * mm, "radius": 5.72 * mm});
            skSolve(sketch);
        }
        {
            var Q0;
            Q0=makeQuery(id+"F51.imprint","IMPRINT",FACE,{"disambiguationData":[TD([[makeQuery(id+"F51.imprint","IMPRINT",EDGE,{"derivedFrom":sQuery(id+"F51.wireOp",EDGE,"E60")}),1.0]])]});
            var Q1;
            Q1=makeQuery(id+"F51.imprint","IMPRINT",FACE,{"disambiguationData":[TD([[makeQuery(id+"F51.imprint","IMPRINT",EDGE,{"derivedFrom":sQuery(id+"F51.wireOp",EDGE,"E61")}),1.0]])]});
            extrude(context, id + "F52", {"entities" : qUnion([Q0, Q1]), "operationType" : NewBodyOperationType.ADD, "depth" : 12.7 * mm, "offsetDistance" : 25.4 * mm});
        }
        {
            var Q0;
            Q0=makeQuery(id+"F52.opExtrude","CAP_FACE",FACE,{"disambiguationData":[OSD([sQuery(id+"F51.wireOp",EDGE,"E60")])],"isStart":false});
            var sketch = newSketch(context, id + "F53", { "sketchPlane" : qUnion([Q0])});
            skCircle(sketch, "E62.0", {"center": v(-6.4, 17.36) * mm, "radius": 4.7 * mm});
            skCircle(sketch, "E63.0", {"center": v(6.26, 17.36) * mm, "radius": 4.7 * mm});
            skSolve(sketch);
        }
        {
            var Q0;
            Q0=makeQuery(id+"F53.imprint","IMPRINT",FACE,{"disambiguationData":[TD([[makeQuery(id+"F53.imprint","IMPRINT",EDGE,{"derivedFrom":sQuery(id+"F53.wireOp",EDGE,"E62.0")}),1.0]])]});
            var Q1;
            Q1=makeQuery(id+"F53.imprint","IMPRINT",FACE,{"disambiguationData":[TD([[makeQuery(id+"F53.imprint","IMPRINT",EDGE,{"derivedFrom":sQuery(id+"F53.wireOp",EDGE,"E63.0")}),1.0]])]});
            extrude(context, id + "F54", {"entities" : qUnion([Q0, Q1]), "operationType" : NewBodyOperationType.REMOVE, "oppositeDirection" : true, "depth" : 12.7 * mm, "offsetDistance" : 25.4 * mm});
        }
        {
            var Q0;
            Q0=makeQuery(id+"F52.opExtrude","CAP_EDGE",EDGE,{"disambiguationData":[OSD([sQuery(id+"F51.wireOp",EDGE,"E60")])],"isStart":false});
            var Q1;
            Q1=makeQuery(id+"F52.opExtrude","CAP_EDGE",EDGE,{"disambiguationData":[OSD([sQuery(id+"F51.wireOp",EDGE,"E61")])],"isStart":false});
            fillet(context, id + "F55", {"entities" : qUnion([Q0, Q1]), "radius" : 5.08 * mm, "tangentPropagation" : true, "allowEdgeOverflow" : false});
        }
        {
            var Q0;
            Q0=qCreatedBy(id+"F50.planeOp",FACE);
            var sketch = newSketch(context, id + "F56", { "sketchPlane" : qUnion([Q0])});
            skCircle(sketch, "E64.0", {"center": v(-6.4, 17.36) * mm, "radius": 1.65 * mm});
            skCircle(sketch, "E65.0", {"center": v(6.26, 17.36) * mm, "radius": 1.65 * mm});
            skCircle(sketch, "E66.cCircle", {"center": v(6.26, 17.36) * mm, "radius": 1.65 * mm, "construction": true});
            skCircle(sketch, "E67.cCircle", {"center": v(-6.4, 17.36) * mm, "radius": 1.65 * mm, "construction": true});
            skLineSegment(sketch, "E67.0", {"start": v(-5.65, 18.89) * mm, "end": v(-5.02, 18.37) * mm});
            skLineSegment(sketch, "E67.1", {"start": v(-5.02, 18.37) * mm, "end": v(-4.71, 17.61) * mm});
            skLineSegment(sketch, "E67.2", {"start": v(-4.71, 17.61) * mm, "end": v(-4.79, 16.8) * mm});
            skLineSegment(sketch, "E67.3", {"start": v(-4.79, 16.8) * mm, "end": v(-5.23, 16.12) * mm});
            skLineSegment(sketch, "E67.4", {"start": v(-5.23, 16.12) * mm, "end": v(-5.94, 15.72) * mm});
            skLineSegment(sketch, "E67.5", {"start": v(-5.94, 15.72) * mm, "end": v(-6.76, 15.7) * mm});
            skLineSegment(sketch, "E67.6", {"start": v(-6.76, 15.7) * mm, "end": v(-7.49, 16.06) * mm});
            skLineSegment(sketch, "E67.7", {"start": v(-7.49, 16.06) * mm, "end": v(-7.97, 16.72) * mm});
            skLineSegment(sketch, "E67.8", {"start": v(-7.97, 16.72) * mm, "end": v(-8.09, 17.52) * mm});
            skLineSegment(sketch, "E67.9", {"start": v(-8.09, 17.52) * mm, "end": v(-7.82, 18.3) * mm});
            skLineSegment(sketch, "E67.10", {"start": v(-7.82, 18.3) * mm, "end": v(-7.23, 18.85) * mm});
            skLineSegment(sketch, "E67.11", {"start": v(-7.23, 18.85) * mm, "end": v(-6.44, 19.06) * mm});
            skLineSegment(sketch, "E67.12", {"start": v(-6.44, 19.06) * mm, "end": v(-5.65, 18.89) * mm});
            skPoint(sketch, "E67.0.midPoint", {"position": v(-5.33, 18.63) * mm});
            skLineSegment(sketch, "E68.0", {"start": v(7.31, 18.7) * mm, "end": v(7.81, 18.06) * mm});
            skLineSegment(sketch, "E68.1", {"start": v(7.81, 18.06) * mm, "end": v(7.96, 17.26) * mm});
            skLineSegment(sketch, "E68.2", {"start": v(7.96, 17.26) * mm, "end": v(7.71, 16.48) * mm});
            skLineSegment(sketch, "E68.3", {"start": v(7.71, 16.48) * mm, "end": v(7.14, 15.9) * mm});
            skLineSegment(sketch, "E68.4", {"start": v(7.14, 15.9) * mm, "end": v(6.36, 15.66) * mm});
            skLineSegment(sketch, "E68.5", {"start": v(6.36, 15.66) * mm, "end": v(5.56, 15.81) * mm});
            skLineSegment(sketch, "E68.6", {"start": v(5.56, 15.81) * mm, "end": v(4.92, 16.32) * mm});
            skLineSegment(sketch, "E68.7", {"start": v(4.92, 16.32) * mm, "end": v(4.59, 17.06) * mm});
            skLineSegment(sketch, "E68.8", {"start": v(4.59, 17.06) * mm, "end": v(4.64, 17.87) * mm});
            skLineSegment(sketch, "E68.9", {"start": v(4.64, 17.87) * mm, "end": v(5.06, 18.57) * mm});
            skLineSegment(sketch, "E68.10", {"start": v(5.06, 18.57) * mm, "end": v(5.76, 18.99) * mm});
            skLineSegment(sketch, "E68.11", {"start": v(5.76, 18.99) * mm, "end": v(6.57, 19.03) * mm});
            skLineSegment(sketch, "E68.12", {"start": v(6.57, 19.03) * mm, "end": v(7.31, 18.7) * mm});
            skPoint(sketch, "E68.0.midPoint", {"position": v(7.56, 18.38) * mm});
            skSolve(sketch);
        }
        {
            var Q0;
            {var subQ0=sQuery(id+"F56.wireOp",EDGE,"e949f48e-603b-4aaa-9e59-412208b0850a.0");var subQ1=sQuery(id+"F56.wireOp",EDGE,"E64.0");var subQ2=makeQuery(id+"F56.imprint","INTERSECT",VERTEX,{"derivedFrom":[subQ1,subQ0]});Q0=makeQuery(id+"F56.imprint","IMPRINT",FACE,{"disambiguationData":[TD([[makeQuery(id+"F56.imprint","IMPRINT",EDGE,{"disambiguationData":[TD([[subQ2,1.0]])],"derivedFrom":subQ1}),-1.0]])]});}
            var Q1;
            {var subQ0=sQuery(id+"F56.wireOp",EDGE,"e949f48e-603b-4aaa-9e59-412208b0850a.7");var subQ1=sQuery(id+"F56.wireOp",EDGE,"E64.0");var subQ2=makeQuery(id+"F56.imprint","INTERSECT",VERTEX,{"derivedFrom":[subQ1,subQ0]});Q1=makeQuery(id+"F56.imprint","IMPRINT",FACE,{"disambiguationData":[TD([[makeQuery(id+"F56.imprint","IMPRINT",EDGE,{"disambiguationData":[TD([[subQ2,1.0]])],"derivedFrom":subQ1}),-1.0]])]});}
            var Q2;
            {var subQ0=sQuery(id+"F56.wireOp",EDGE,"e949f48e-603b-4aaa-9e59-412208b0850a.6");var subQ1=sQuery(id+"F56.wireOp",EDGE,"E64.0");var subQ2=makeQuery(id+"F56.imprint","INTERSECT",VERTEX,{"derivedFrom":[subQ1,subQ0]});Q2=makeQuery(id+"F56.imprint","IMPRINT",FACE,{"disambiguationData":[TD([[makeQuery(id+"F56.imprint","IMPRINT",EDGE,{"disambiguationData":[TD([[subQ2,-1.0]])],"derivedFrom":subQ1}),-1.0]])]});}
            var Q3;
            {var subQ0=sQuery(id+"F56.wireOp",EDGE,"e949f48e-603b-4aaa-9e59-412208b0850a.5");var subQ1=sQuery(id+"F56.wireOp",EDGE,"E64.0");var subQ2=makeQuery(id+"F56.imprint","INTERSECT",VERTEX,{"derivedFrom":[subQ1,subQ0]});Q3=makeQuery(id+"F56.imprint","IMPRINT",FACE,{"disambiguationData":[TD([[makeQuery(id+"F56.imprint","IMPRINT",EDGE,{"disambiguationData":[TD([[subQ2,-1.0]])],"derivedFrom":subQ1}),-1.0]])]});}
            var Q4;
            {var subQ0=sQuery(id+"F56.wireOp",EDGE,"e949f48e-603b-4aaa-9e59-412208b0850a.4");var subQ1=sQuery(id+"F56.wireOp",EDGE,"E64.0");var subQ2=makeQuery(id+"F56.imprint","INTERSECT",VERTEX,{"derivedFrom":[subQ1,subQ0]});Q4=makeQuery(id+"F56.imprint","IMPRINT",FACE,{"disambiguationData":[TD([[makeQuery(id+"F56.imprint","IMPRINT",EDGE,{"disambiguationData":[TD([[subQ2,-1.0]])],"derivedFrom":subQ1}),-1.0]])]});}
            var Q5;
            {var subQ0=sQuery(id+"F56.wireOp",EDGE,"e949f48e-603b-4aaa-9e59-412208b0850a.3");var subQ1=sQuery(id+"F56.wireOp",EDGE,"E64.0");var subQ2=makeQuery(id+"F56.imprint","INTERSECT",VERTEX,{"derivedFrom":[subQ1,subQ0]});Q5=makeQuery(id+"F56.imprint","IMPRINT",FACE,{"disambiguationData":[TD([[makeQuery(id+"F56.imprint","IMPRINT",EDGE,{"disambiguationData":[TD([[subQ2,-1.0]])],"derivedFrom":subQ1}),-1.0]])]});}
            var Q6;
            {var subQ0=sQuery(id+"F56.wireOp",EDGE,"e949f48e-603b-4aaa-9e59-412208b0850a.2");var subQ1=sQuery(id+"F56.wireOp",EDGE,"E64.0");var subQ2=makeQuery(id+"F56.imprint","INTERSECT",VERTEX,{"derivedFrom":[subQ1,subQ0]});Q6=makeQuery(id+"F56.imprint","IMPRINT",FACE,{"disambiguationData":[TD([[makeQuery(id+"F56.imprint","IMPRINT",EDGE,{"disambiguationData":[TD([[subQ2,-1.0]])],"derivedFrom":subQ1}),-1.0]])]});}
            var Q7;
            {var subQ0=sQuery(id+"F56.wireOp",EDGE,"E66.5");var subQ1=sQuery(id+"F56.wireOp",EDGE,"E65.0");var subQ2=makeQuery(id+"F56.imprint","INTERSECT",VERTEX,{"derivedFrom":[subQ1,subQ0]});Q7=makeQuery(id+"F56.imprint","IMPRINT",FACE,{"disambiguationData":[TD([[makeQuery(id+"F56.imprint","IMPRINT",EDGE,{"disambiguationData":[TD([[subQ2,-1.0]])],"derivedFrom":subQ1}),-1.0]])]});}
            var Q8;
            {var subQ0=sQuery(id+"F56.wireOp",EDGE,"E66.6");var subQ1=sQuery(id+"F56.wireOp",EDGE,"E65.0");var subQ2=makeQuery(id+"F56.imprint","INTERSECT",VERTEX,{"derivedFrom":[subQ1,subQ0]});Q8=makeQuery(id+"F56.imprint","IMPRINT",FACE,{"disambiguationData":[TD([[makeQuery(id+"F56.imprint","IMPRINT",EDGE,{"disambiguationData":[TD([[subQ2,-1.0]])],"derivedFrom":subQ1}),-1.0]])]});}
            var Q9;
            {var subQ0=sQuery(id+"F56.wireOp",EDGE,"E66.7");var subQ1=sQuery(id+"F56.wireOp",EDGE,"E65.0");var subQ2=makeQuery(id+"F56.imprint","INTERSECT",VERTEX,{"derivedFrom":[subQ1,subQ0]});Q9=makeQuery(id+"F56.imprint","IMPRINT",FACE,{"disambiguationData":[TD([[makeQuery(id+"F56.imprint","IMPRINT",EDGE,{"disambiguationData":[TD([[subQ2,-1.0]])],"derivedFrom":subQ1}),-1.0]])]});}
            var Q10;
            {var subQ0=sQuery(id+"F56.wireOp",EDGE,"E66.7");var subQ1=sQuery(id+"F56.wireOp",EDGE,"E65.0");var subQ2=makeQuery(id+"F56.imprint","INTERSECT",VERTEX,{"derivedFrom":[subQ1,subQ0]});Q10=makeQuery(id+"F56.imprint","IMPRINT",FACE,{"disambiguationData":[TD([[makeQuery(id+"F56.imprint","IMPRINT",EDGE,{"disambiguationData":[TD([[subQ2,1.0]])],"derivedFrom":subQ1}),-1.0]])]});}
            var Q11;
            {var subQ0=sQuery(id+"F56.wireOp",EDGE,"E66.0");var subQ1=sQuery(id+"F56.wireOp",EDGE,"E65.0");var subQ2=makeQuery(id+"F56.imprint","INTERSECT",VERTEX,{"derivedFrom":[subQ1,subQ0]});Q11=makeQuery(id+"F56.imprint","IMPRINT",FACE,{"disambiguationData":[TD([[makeQuery(id+"F56.imprint","IMPRINT",EDGE,{"disambiguationData":[TD([[subQ2,1.0]])],"derivedFrom":subQ1}),-1.0]])]});}
            var Q12;
            {var subQ0=sQuery(id+"F56.wireOp",EDGE,"E66.2");var subQ1=sQuery(id+"F56.wireOp",EDGE,"E65.0");var subQ2=makeQuery(id+"F56.imprint","INTERSECT",VERTEX,{"derivedFrom":[subQ1,subQ0]});Q12=makeQuery(id+"F56.imprint","IMPRINT",FACE,{"disambiguationData":[TD([[makeQuery(id+"F56.imprint","IMPRINT",EDGE,{"disambiguationData":[TD([[subQ2,-1.0]])],"derivedFrom":subQ1}),-1.0]])]});}
            var Q13;
            {var subQ0=sQuery(id+"F56.wireOp",EDGE,"E66.3");var subQ1=sQuery(id+"F56.wireOp",EDGE,"E65.0");var subQ2=makeQuery(id+"F56.imprint","INTERSECT",VERTEX,{"derivedFrom":[subQ1,subQ0]});Q13=makeQuery(id+"F56.imprint","IMPRINT",FACE,{"disambiguationData":[TD([[makeQuery(id+"F56.imprint","IMPRINT",EDGE,{"disambiguationData":[TD([[subQ2,-1.0]])],"derivedFrom":subQ1}),-1.0]])]});}
            var Q14;
            {var subQ0=sQuery(id+"F56.wireOp",EDGE,"E66.4");var subQ1=sQuery(id+"F56.wireOp",EDGE,"E65.0");var subQ2=makeQuery(id+"F56.imprint","INTERSECT",VERTEX,{"derivedFrom":[subQ1,subQ0]});Q14=makeQuery(id+"F56.imprint","IMPRINT",FACE,{"disambiguationData":[TD([[makeQuery(id+"F56.imprint","IMPRINT",EDGE,{"disambiguationData":[TD([[subQ2,-1.0]])],"derivedFrom":subQ1}),-1.0]])]});}
            var Q15;
            {var subQ0=sQuery(id+"F56.wireOp",EDGE,"E65.0");var subQ4=makeQuery(id+"F56.imprint","INTERSECT",VERTEX,{"derivedFrom":[subQ0,sQuery(id+"F56.wireOp",EDGE,"E66.7")]});Q15=makeQuery(id+"F56.imprint","IMPRINT",FACE,{"disambiguationData":[TD([[makeQuery(id+"F56.imprint","IMPRINT",EDGE,{"disambiguationData":[TD([[subQ4,1.0]])],"derivedFrom":subQ0}),1.0]])]});}
            var Q16;
            {var subQ0=sQuery(id+"F56.wireOp",EDGE,"e949f48e-603b-4aaa-9e59-412208b0850a.7");var subQ1=sQuery(id+"F56.wireOp",EDGE,"E64.0");var subQ2=makeQuery(id+"F56.imprint","INTERSECT",VERTEX,{"derivedFrom":[subQ1,subQ0]});Q16=makeQuery(id+"F56.imprint","IMPRINT",FACE,{"disambiguationData":[TD([[makeQuery(id+"F56.imprint","IMPRINT",EDGE,{"disambiguationData":[TD([[subQ2,-1.0]])],"derivedFrom":subQ1}),-1.0]])]});}
            var Q17;
            {var subQ0=sQuery(id+"F56.wireOp",EDGE,"E64.0");var subQ4=makeQuery(id+"F56.imprint","INTERSECT",VERTEX,{"derivedFrom":[subQ0,sQuery(id+"F56.wireOp",EDGE,"e949f48e-603b-4aaa-9e59-412208b0850a.7")]});Q17=makeQuery(id+"F56.imprint","IMPRINT",FACE,{"disambiguationData":[TD([[makeQuery(id+"F56.imprint","IMPRINT",EDGE,{"disambiguationData":[TD([[subQ4,1.0]])],"derivedFrom":subQ0}),1.0]])]});}
            extrude(context, id + "F57", {"entities" : qUnion([Q0, Q1, Q2, Q3, Q4, Q5, Q6, Q7, Q8, Q9, Q10, Q11, Q12, Q13, Q14, Q15, Q16, Q17]), "depth" : 7.62 * mm, "offsetDistance" : 25.4 * mm});
        }
        {
            var Q0;
            Q0=makeQuery(id+"F57.opExtrude","CAP_FACE",FACE,{"disambiguationData":[OSD([sQuery(id+"F56.wireOp",EDGE,"E67.0"),sQuery(id+"F56.wireOp",EDGE,"E67.1"),sQuery(id+"F56.wireOp",EDGE,"E67.2"),sQuery(id+"F56.wireOp",EDGE,"E67.3"),sQuery(id+"F56.wireOp",EDGE,"E67.4"),sQuery(id+"F56.wireOp",EDGE,"E67.5"),sQuery(id+"F56.wireOp",EDGE,"E67.6"),sQuery(id+"F56.wireOp",EDGE,"E67.7"),sQuery(id+"F56.wireOp",EDGE,"E67.8"),sQuery(id+"F56.wireOp",EDGE,"E67.9"),sQuery(id+"F56.wireOp",EDGE,"E67.10"),sQuery(id+"F56.wireOp",EDGE,"E67.11"),sQuery(id+"F56.wireOp",EDGE,"E67.12")])],"isStart":true});
            var sketch = newSketch(context, id + "F58", { "sketchPlane" : qUnion([Q0])});
            skCircle(sketch, "E69", {"center": v(6.36, 17.39) * mm, "radius": 1.68 * mm});
            skPoint(sketch, "E69.first.point", {"position": v(6.44, 19.06) * mm});
            skPoint(sketch, "E69.second.point", {"position": v(6.44, 15.7) * mm});
            skPoint(sketch, "E69.third.point", {"position": v(4.79, 16.8) * mm});
            skSolve(sketch);
        }
        {
            var Q0;
            Q0=makeQuery(id+"F58.imprint","IMPRINT",FACE,{"disambiguationData":[TD([[makeQuery(id+"F58.imprint","IMPRINT",EDGE,{"derivedFrom":makeQuery(id+"F57.opExtrude","CAP_EDGE",EDGE,{"disambiguationData":[OSD([sQuery(id+"F56.wireOp",EDGE,"E67.0")])],"isStart":true})}),1.0]])]});
            extrude(context, id + "F59", {"entities" : qUnion([Q0]), "operationType" : NewBodyOperationType.ADD, "depth" : 3.45 * mm, "offsetDistance" : 25.4 * mm, "hasDraft" : true, "draftAngle" : 25 * degree, "draftPullDirection" : true});
        }
        {
            var Q0;
            Q0=makeQuery(id+"F57.opExtrude","CAP_FACE",FACE,{"disambiguationData":[OSD([sQuery(id+"F56.wireOp",EDGE,"E68.0"),sQuery(id+"F56.wireOp",EDGE,"E68.1"),sQuery(id+"F56.wireOp",EDGE,"E68.2"),sQuery(id+"F56.wireOp",EDGE,"E68.3"),sQuery(id+"F56.wireOp",EDGE,"E68.4"),sQuery(id+"F56.wireOp",EDGE,"E68.5"),sQuery(id+"F56.wireOp",EDGE,"E68.6"),sQuery(id+"F56.wireOp",EDGE,"E68.7"),sQuery(id+"F56.wireOp",EDGE,"E68.8"),sQuery(id+"F56.wireOp",EDGE,"E68.9"),sQuery(id+"F56.wireOp",EDGE,"E68.10"),sQuery(id+"F56.wireOp",EDGE,"E68.11"),sQuery(id+"F56.wireOp",EDGE,"E68.12")])],"isStart":true});
            var sketch = newSketch(context, id + "F60", { "sketchPlane" : qUnion([Q0])});
            skCircle(sketch, "E70", {"center": v(-6.26, 17.36) * mm, "radius": 1.7 * mm});
            skPoint(sketch, "E70.first.point", {"position": v(-5.76, 18.99) * mm});
            skPoint(sketch, "E70.second.point", {"position": v(-6.36, 15.66) * mm});
            skPoint(sketch, "E70.third.point", {"position": v(-7.71, 16.48) * mm});
            skSolve(sketch);
        }
        {
            var Q0;
            Q0=makeQuery(id+"F60.imprint","IMPRINT",FACE,{"disambiguationData":[TD([[makeQuery(id+"F60.imprint","IMPRINT",EDGE,{"derivedFrom":makeQuery(id+"F57.opExtrude","CAP_EDGE",EDGE,{"disambiguationData":[OSD([sQuery(id+"F56.wireOp",EDGE,"E68.0")])],"isStart":true})}),1.0]])]});
            extrude(context, id + "F61", {"entities" : qUnion([Q0]), "operationType" : NewBodyOperationType.ADD, "depth" : 3.45 * mm, "offsetDistance" : 25.4 * mm, "hasDraft" : true, "draftAngle" : 25 * degree, "draftPullDirection" : true});
        }
        {
            var Q0;
            Q0=makeQuery(id+"F57.opExtrude","CAP_FACE",FACE,{"disambiguationData":[OSD([sQuery(id+"F56.wireOp",EDGE,"E67.0"),sQuery(id+"F56.wireOp",EDGE,"E67.1"),sQuery(id+"F56.wireOp",EDGE,"E67.2"),sQuery(id+"F56.wireOp",EDGE,"E67.3"),sQuery(id+"F56.wireOp",EDGE,"E67.4"),sQuery(id+"F56.wireOp",EDGE,"E67.5"),sQuery(id+"F56.wireOp",EDGE,"E67.6"),sQuery(id+"F56.wireOp",EDGE,"E67.7"),sQuery(id+"F56.wireOp",EDGE,"E67.8"),sQuery(id+"F56.wireOp",EDGE,"E67.9"),sQuery(id+"F56.wireOp",EDGE,"E67.10"),sQuery(id+"F56.wireOp",EDGE,"E67.11"),sQuery(id+"F56.wireOp",EDGE,"E67.12")])],"isStart":false});
            var sketch = newSketch(context, id + "F62", { "sketchPlane" : qUnion([Q0])});
            skCircle(sketch, "E71", {"center": v(-6.4, 17.36) * mm, "radius": 1.7 * mm});
            skPoint(sketch, "E71.first.point", {"position": v(-6.44, 19.06) * mm});
            skPoint(sketch, "E71.second.point", {"position": v(-5.23, 16.12) * mm});
            skPoint(sketch, "E71.third.point", {"position": v(-7.49, 16.06) * mm});
            skSolve(sketch);
        }
        {
            var Q0;
            Q0=makeQuery(id+"F62.imprint","IMPRINT",FACE,{"disambiguationData":[TD([[makeQuery(id+"F62.imprint","IMPRINT",EDGE,{"derivedFrom":makeQuery(id+"F57.opExtrude","CAP_EDGE",EDGE,{"disambiguationData":[OSD([sQuery(id+"F56.wireOp",EDGE,"E67.0")])],"isStart":false})}),-1.0]])]});
            extrude(context, id + "F63", {"entities" : qUnion([Q0]), "operationType" : NewBodyOperationType.ADD, "depth" : 7.37 * mm, "offsetDistance" : 25.4 * mm, "hasDraft" : true, "draftAngle" : 4 * degree, "draftPullDirection" : true});
        }
        {
            var Q0;
            Q0=makeQuery(id+"F57.opExtrude","CAP_FACE",FACE,{"disambiguationData":[OSD([sQuery(id+"F56.wireOp",EDGE,"E68.0"),sQuery(id+"F56.wireOp",EDGE,"E68.1"),sQuery(id+"F56.wireOp",EDGE,"E68.2"),sQuery(id+"F56.wireOp",EDGE,"E68.3"),sQuery(id+"F56.wireOp",EDGE,"E68.4"),sQuery(id+"F56.wireOp",EDGE,"E68.5"),sQuery(id+"F56.wireOp",EDGE,"E68.6"),sQuery(id+"F56.wireOp",EDGE,"E68.7"),sQuery(id+"F56.wireOp",EDGE,"E68.8"),sQuery(id+"F56.wireOp",EDGE,"E68.9"),sQuery(id+"F56.wireOp",EDGE,"E68.10"),sQuery(id+"F56.wireOp",EDGE,"E68.11"),sQuery(id+"F56.wireOp",EDGE,"E68.12")])],"isStart":false});
            var sketch = newSketch(context, id + "F64", { "sketchPlane" : qUnion([Q0])});
            skCircle(sketch, "E72", {"center": v(6.26, 17.36) * mm, "radius": 1.7 * mm});
            skPoint(sketch, "E72.first.point", {"position": v(6.57, 19.03) * mm});
            skPoint(sketch, "E72.second.point", {"position": v(7.14, 15.9) * mm});
            skPoint(sketch, "E72.third.point", {"position": v(5.56, 15.81) * mm});
            skSolve(sketch);
        }
        {
            var Q0;
            Q0=makeQuery(id+"F64.imprint","IMPRINT",FACE,{"disambiguationData":[TD([[makeQuery(id+"F64.imprint","IMPRINT",EDGE,{"derivedFrom":makeQuery(id+"F57.opExtrude","CAP_EDGE",EDGE,{"disambiguationData":[OSD([sQuery(id+"F56.wireOp",EDGE,"E68.0")])],"isStart":false})}),-1.0]])]});
            extrude(context, id + "F65", {"entities" : qUnion([Q0]), "operationType" : NewBodyOperationType.ADD, "depth" : 7.37 * mm, "offsetDistance" : 25.4 * mm, "hasDraft" : true, "draftAngle" : 4 * degree, "draftPullDirection" : true});
        }
        {
            var Q0;
            Q0=makeQuery(id+"F57.opExtrude","SWEPT_FACE",FACE,{"disambiguationData":[OSD([sQuery(id+"F56.wireOp",EDGE,"E68.12")])]});
            var sketch = newSketch(context, id + "F66", { "sketchPlane" : qUnion([Q0])});
            skPoint(sketch, "E73.5.internal.snap0", {"position": v(-1.46, -86.36) * mm});
            skFitSpline(sketch, "E73", {"points": [v(-1.12, -93.98) * mm, v(-1.87, -91.27) * mm, v(-1.46, -86.36) * mm, v(-1.74, -89.19) * mm, v(-1.73, -91) * mm, v(-1.46, -91.64) * mm, v(-1.12, -93.98) * mm]});
            skPoint(sketch, "E74", {"position": v(-1.62, -87.99) * mm});
            skPoint(sketch, "E75", {"position": v(-1.8, -90.17) * mm});
            skPoint(sketch, "E76", {"position": v(-1.2, -92.8) * mm});
            skFitSpline(sketch, "E77", {"points": [v(-0.27, -94.87) * mm, v(-1.02, -92.16) * mm, v(-0.62, -87.25) * mm, v(-0.9, -90.07) * mm, v(-0.88, -91.89) * mm, v(-0.62, -92.52) * mm, v(-0.27, -94.87) * mm]});
            skSolve(sketch);
        }
        {
            var Q0;
            {var subQ0=sQuery(id+"F66.wireOp",EDGE,"E73");var subQ1=sQuery(id+"F56.wireOp",EDGE,"E68.12");var subQ5=makeQuery(id+"F65.boolean.opBoolean","MERGE",EDGE,{"derivedFrom":[makeQuery(id+"F57.opExtrude","CAP_EDGE",EDGE,{"disambiguationData":[OSD([subQ1])],"isStart":false}),makeQuery(id+"F65.opExtrude","CAP_EDGE",EDGE,{"disambiguationData":[OSD([subQ1])],"isStart":true})]});var subQ10=makeQuery(id+"F66.imprint","INTERSECT",VERTEX,{"disambiguationData":[OD(0.0)],"derivedFrom":[subQ5,subQ0]});Q0=makeQuery(id+"F66.imprint","IMPRINT",FACE,{"disambiguationData":[TD([[makeQuery(id+"F66.imprint","IMPRINT",EDGE,{"disambiguationData":[TD([[subQ10,-1.0]])],"derivedFrom":subQ0}),-1.0]])]});}
            extrude(context, id + "F67", {"entities" : qUnion([Q0]), "operationType" : NewBodyOperationType.ADD, "depth" : 2.8 * mm, "offsetDistance" : 25.4 * mm});
        }
        {
            var Q0;
            Q0=makeQuery(id+"F57.opExtrude","SWEPT_FACE",FACE,{"disambiguationData":[OSD([sQuery(id+"F56.wireOp",EDGE,"E68.0")])]});
            var sketch = newSketch(context, id + "F68", { "sketchPlane" : qUnion([Q0])});
            skFitSpline(sketch, "E78", {"points": [v(-18.96, 81.79) * mm, v(-19.7, 84.5) * mm, v(-19.3, 89.4) * mm, v(-19.58, 86.58) * mm, v(-19.57, 84.77) * mm, v(-19.3, 84.13) * mm, v(-18.96, 81.79) * mm]});
            skFitSpline(sketch, "E79", {"points": [v(-93.9, 9.5) * mm, v(-91.2, 10.25) * mm, v(-86.29, 9.84) * mm, v(-89.12, 10.12) * mm, v(-90.93, 10.11) * mm, v(-91.56, 9.84) * mm, v(-93.9, 9.5) * mm]});
            skSolve(sketch);
        }
        {
            var Q0;
            {var subQ0=sQuery(id+"F68.wireOp",EDGE,"E79");var subQ1=sQuery(id+"F56.wireOp",EDGE,"E68.0");var subQ2=makeQuery(id+"F57.opExtrude","SWEPT_EDGE",EDGE,{"disambiguationData":[OSD([subQ1,sQuery(id+"F56.wireOp",EDGE,"E68.12")])]});var subQ3=makeQuery(id+"F68.imprint","INTERSECT",VERTEX,{"disambiguationData":[OD(0.0)],"derivedFrom":[subQ2,subQ0]});Q0=makeQuery(id+"F68.imprint","IMPRINT",FACE,{"disambiguationData":[TD([[makeQuery(id+"F68.imprint","IMPRINT",EDGE,{"disambiguationData":[TD([[subQ3,-1.0]])],"derivedFrom":subQ0}),-1.0]])]});}
            extrude(context, id + "F69", {"entities" : qUnion([Q0]), "operationType" : NewBodyOperationType.ADD, "depth" : 2.8 * mm, "offsetDistance" : 25.4 * mm});
        }
        {
            var Q0;
            Q0=makeQuery(id+"F57.opExtrude","SWEPT_FACE",FACE,{"disambiguationData":[OSD([sQuery(id+"F56.wireOp",EDGE,"E68.1")])]});
            var sketch = newSketch(context, id + "F70", { "sketchPlane" : qUnion([Q0])});
            skFitSpline(sketch, "E80", {"points": [v(-93.98, 15.56) * mm, v(-91.28, 16.34) * mm, v(-86.36, 15.99) * mm, v(-89.2, 16.24) * mm, v(-91, 16.2) * mm, v(-91.64, 15.93) * mm, v(-93.98, 15.56) * mm]});
            skSolve(sketch);
        }
        {
            var Q0;
            {var subQ0=sQuery(id+"F70.wireOp",EDGE,"E80");var subQ1=sQuery(id+"F56.wireOp",EDGE,"E68.1");var subQ2=makeQuery(id+"F65.boolean.opBoolean","MERGE",EDGE,{"derivedFrom":[makeQuery(id+"F57.opExtrude","CAP_EDGE",EDGE,{"disambiguationData":[OSD([subQ1])],"isStart":false}),makeQuery(id+"F65.opExtrude","CAP_EDGE",EDGE,{"disambiguationData":[OSD([subQ1])],"isStart":true})]});var subQ9=makeQuery(id+"F70.imprint","INTERSECT",VERTEX,{"derivedFrom":[subQ2,subQ0]});Q0=makeQuery(id+"F70.imprint","IMPRINT",FACE,{"disambiguationData":[TD([[makeQuery(id+"F70.imprint","IMPRINT",EDGE,{"disambiguationData":[TD([[subQ9,-1.0]])],"derivedFrom":subQ0}),-1.0]])]});}
            extrude(context, id + "F71", {"entities" : qUnion([Q0]), "operationType" : NewBodyOperationType.ADD, "depth" : 2.8 * mm, "offsetDistance" : 25.4 * mm});
        }
        {
            var Q0;
            Q0=makeQuery(id+"F57.opExtrude","SWEPT_FACE",FACE,{"disambiguationData":[OSD([sQuery(id+"F56.wireOp",EDGE,"E68.2")])]});
            var sketch = newSketch(context, id + "F72", { "sketchPlane" : qUnion([Q0])});
            skFitSpline(sketch, "E81", {"points": [v(55.89, -485.43) * mm, v(55.14, -482.72) * mm, v(55.55, -477.81) * mm, v(55.27, -480.64) * mm, v(55.28, -482.45) * mm, v(55.55, -483.09) * mm, v(55.89, -485.43) * mm]});
            skFitSpline(sketch, "E82", {"points": [v(-93.8, 18.03) * mm, v(-91.1, 18.8) * mm, v(-86.19, 18.42) * mm, v(-89.02, 18.68) * mm, v(-90.83, 18.66) * mm, v(-91.46, 18.39) * mm, v(-93.8, 18.03) * mm]});
            skSolve(sketch);
        }
        {
            var Q0;
            {var subQ0=sQuery(id+"F72.wireOp",EDGE,"E82");var subQ1=sQuery(id+"F56.wireOp",EDGE,"E68.2");var subQ2=makeQuery(id+"F61.boolean.opBoolean","MERGE",EDGE,{"derivedFrom":[makeQuery(id+"F57.opExtrude","CAP_EDGE",EDGE,{"disambiguationData":[OSD([subQ1])],"isStart":true}),makeQuery(id+"F61.opExtrude","CAP_EDGE",EDGE,{"disambiguationData":[OSD([subQ1])],"isStart":true})]});var subQ3=makeQuery(id+"F72.imprint","INTERSECT",VERTEX,{"disambiguationData":[OD(0.0)],"derivedFrom":[subQ2,subQ0]});Q0=makeQuery(id+"F72.imprint","IMPRINT",FACE,{"disambiguationData":[TD([[makeQuery(id+"F72.imprint","IMPRINT",EDGE,{"disambiguationData":[TD([[subQ3,1.0]])],"derivedFrom":subQ0}),-1.0]])]});}
            extrude(context, id + "F73", {"entities" : qUnion([Q0]), "operationType" : NewBodyOperationType.ADD, "depth" : 2.8 * mm, "offsetDistance" : 25.4 * mm});
        }
        {
            var Q0;
            Q0=makeQuery(id+"F57.opExtrude","SWEPT_FACE",FACE,{"disambiguationData":[OSD([sQuery(id+"F56.wireOp",EDGE,"E68.3")])]});
            var sketch = newSketch(context, id + "F74", { "sketchPlane" : qUnion([Q0])});
            skFitSpline(sketch, "E83", {"points": [v(16.35, 93.98) * mm, v(17.1, 91.27) * mm, v(16.69, 86.36) * mm, v(16.97, 89.19) * mm, v(16.96, 91) * mm, v(16.69, 91.64) * mm, v(16.35, 93.98) * mm]});
            skSolve(sketch);
        }
        {
            var Q0;
            {var subQ0=sQuery(id+"F74.wireOp",EDGE,"E83");var subQ1=sQuery(id+"F56.wireOp",EDGE,"E68.3");var subQ2=makeQuery(id+"F65.boolean.opBoolean","MERGE",EDGE,{"derivedFrom":[makeQuery(id+"F57.opExtrude","CAP_EDGE",EDGE,{"disambiguationData":[OSD([subQ1])],"isStart":false}),makeQuery(id+"F65.opExtrude","CAP_EDGE",EDGE,{"disambiguationData":[OSD([subQ1])],"isStart":true})]});var subQ3=makeQuery(id+"F74.imprint","INTERSECT",VERTEX,{"disambiguationData":[OD(1.0)],"derivedFrom":[subQ2,subQ0]});Q0=makeQuery(id+"F74.imprint","IMPRINT",FACE,{"disambiguationData":[TD([[makeQuery(id+"F74.imprint","IMPRINT",EDGE,{"disambiguationData":[TD([[subQ3,1.0]])],"derivedFrom":subQ0}),-1.0]])]});}
            extrude(context, id + "F75", {"entities" : qUnion([Q0]), "operationType" : NewBodyOperationType.ADD, "depth" : 2.8 * mm, "offsetDistance" : 25.4 * mm});
        }
        {
            var Q0;
            Q0=makeQuery(id+"F57.opExtrude","SWEPT_FACE",FACE,{"disambiguationData":[OSD([sQuery(id+"F56.wireOp",EDGE,"E68.4")])]});
            var sketch = newSketch(context, id + "F76", { "sketchPlane" : qUnion([Q0])});
            skFitSpline(sketch, "E84", {"points": [v(10.78, 93.98) * mm, v(11.43, 91.25) * mm, v(10.85, 86.35) * mm, v(11.23, 89.17) * mm, v(11.28, 90.98) * mm, v(11.03, 91.63) * mm, v(10.78, 93.98) * mm]});
            skSolve(sketch);
        }
        {
            var Q0;
            {var subQ0=sQuery(id+"F76.wireOp",EDGE,"E84");var subQ1=sQuery(id+"F56.wireOp",EDGE,"E68.4");var subQ2=makeQuery(id+"F65.boolean.opBoolean","MERGE",EDGE,{"derivedFrom":[makeQuery(id+"F57.opExtrude","CAP_EDGE",EDGE,{"disambiguationData":[OSD([subQ1])],"isStart":false}),makeQuery(id+"F65.opExtrude","CAP_EDGE",EDGE,{"disambiguationData":[OSD([subQ1])],"isStart":true})]});var subQ3=makeQuery(id+"F76.imprint","INTERSECT",VERTEX,{"disambiguationData":[OD(0.0)],"derivedFrom":[subQ2,subQ0]});Q0=makeQuery(id+"F76.imprint","IMPRINT",FACE,{"disambiguationData":[TD([[makeQuery(id+"F76.imprint","IMPRINT",EDGE,{"disambiguationData":[TD([[subQ3,-1.0]])],"derivedFrom":subQ0}),-1.0]])]});}
            extrude(context, id + "F77", {"entities" : qUnion([Q0]), "operationType" : NewBodyOperationType.ADD, "depth" : 2.8 * mm, "offsetDistance" : 25.4 * mm});
        }
        {
            var Q0;
            Q0=makeQuery(id+"F57.opExtrude","SWEPT_FACE",FACE,{"disambiguationData":[OSD([sQuery(id+"F56.wireOp",EDGE,"E68.5")])]});
            var sketch = newSketch(context, id + "F78", { "sketchPlane" : qUnion([Q0])});
            skFitSpline(sketch, "E85", {"points": [v(2.62, 93.98) * mm, v(3.33, 91.26) * mm, v(2.86, 86.36) * mm, v(3.17, 89.18) * mm, v(3.18, 91) * mm, v(2.93, 91.63) * mm, v(2.62, 93.98) * mm]});
            skSolve(sketch);
        }
        {
            var Q0;
            {var subQ0=sQuery(id+"F78.wireOp",EDGE,"E85");var subQ1=sQuery(id+"F56.wireOp",EDGE,"E68.5");var subQ2=makeQuery(id+"F65.boolean.opBoolean","MERGE",EDGE,{"derivedFrom":[makeQuery(id+"F57.opExtrude","CAP_EDGE",EDGE,{"disambiguationData":[OSD([subQ1])],"isStart":false}),makeQuery(id+"F65.opExtrude","CAP_EDGE",EDGE,{"disambiguationData":[OSD([subQ1])],"isStart":true})]});var subQ3=makeQuery(id+"F78.imprint","INTERSECT",VERTEX,{"disambiguationData":[OD(0.0)],"derivedFrom":[subQ2,subQ0]});Q0=makeQuery(id+"F78.imprint","IMPRINT",FACE,{"disambiguationData":[TD([[makeQuery(id+"F78.imprint","IMPRINT",EDGE,{"disambiguationData":[TD([[subQ3,-1.0]])],"derivedFrom":subQ0}),-1.0]])]});}
            extrude(context, id + "F79", {"entities" : qUnion([Q0]), "operationType" : NewBodyOperationType.ADD, "depth" : 2.8 * mm, "offsetDistance" : 25.4 * mm});
        }
        {
            var Q0;
            Q0=makeQuery(id+"F57.opExtrude","SWEPT_FACE",FACE,{"disambiguationData":[OSD([sQuery(id+"F56.wireOp",EDGE,"E68.6")])]});
            var sketch = newSketch(context, id + "F80", { "sketchPlane" : qUnion([Q0])});
            skFitSpline(sketch, "E86", {"points": [v(-6.23, 93.98) * mm, v(-5.48, 91.27) * mm, v(-5.89, 86.36) * mm, v(-5.6, 89.19) * mm, v(-5.62, 91) * mm, v(-5.89, 91.64) * mm, v(-6.23, 93.98) * mm]});
            skSolve(sketch);
        }
        {
            var Q0;
            {var subQ0=sQuery(id+"F80.wireOp",EDGE,"E86");var subQ1=sQuery(id+"F56.wireOp",EDGE,"E68.6");var subQ5=makeQuery(id+"F65.boolean.opBoolean","MERGE",EDGE,{"derivedFrom":[makeQuery(id+"F57.opExtrude","CAP_EDGE",EDGE,{"disambiguationData":[OSD([subQ1])],"isStart":false}),makeQuery(id+"F65.opExtrude","CAP_EDGE",EDGE,{"disambiguationData":[OSD([subQ1])],"isStart":true})]});var subQ9=makeQuery(id+"F80.imprint","INTERSECT",VERTEX,{"derivedFrom":[subQ5,subQ0]});Q0=makeQuery(id+"F80.imprint","IMPRINT",FACE,{"disambiguationData":[TD([[makeQuery(id+"F80.imprint","IMPRINT",EDGE,{"disambiguationData":[TD([[subQ9,-1.0]])],"derivedFrom":subQ0}),-1.0]])]});}
            extrude(context, id + "F81", {"entities" : qUnion([Q0]), "operationType" : NewBodyOperationType.ADD, "depth" : 2.8 * mm, "offsetDistance" : 25.4 * mm});
        }
        {
            var Q0;
            Q0=makeQuery(id+"F57.opExtrude","SWEPT_FACE",FACE,{"disambiguationData":[OSD([sQuery(id+"F56.wireOp",EDGE,"E68.7")])]});
            var sketch = newSketch(context, id + "F82", { "sketchPlane" : qUnion([Q0])});
            skFitSpline(sketch, "E87", {"points": [v(93.97, 13.63) * mm, v(91.26, 12.89) * mm, v(86.35, 13.3) * mm, v(89.18, 13.02) * mm, v(91, 13.03) * mm, v(91.63, 13.3) * mm, v(93.97, 13.63) * mm]});
            skSolve(sketch);
        }
        {
            var Q0;
            {var subQ0=sQuery(id+"F82.wireOp",EDGE,"E87");var subQ1=sQuery(id+"F56.wireOp",EDGE,"E68.7");var subQ5=makeQuery(id+"F65.boolean.opBoolean","MERGE",EDGE,{"derivedFrom":[makeQuery(id+"F57.opExtrude","CAP_EDGE",EDGE,{"disambiguationData":[OSD([subQ1])],"isStart":false}),makeQuery(id+"F65.opExtrude","CAP_EDGE",EDGE,{"disambiguationData":[OSD([subQ1])],"isStart":true})]});var subQ10=makeQuery(id+"F82.imprint","INTERSECT",VERTEX,{"disambiguationData":[OD(0.0)],"derivedFrom":[subQ5,subQ0]});Q0=makeQuery(id+"F82.imprint","IMPRINT",FACE,{"disambiguationData":[TD([[makeQuery(id+"F82.imprint","IMPRINT",EDGE,{"disambiguationData":[TD([[subQ10,-1.0]])],"derivedFrom":subQ0}),-1.0]])]});}
            extrude(context, id + "F83", {"entities" : qUnion([Q0]), "operationType" : NewBodyOperationType.ADD, "depth" : 2.8 * mm, "offsetDistance" : 25.4 * mm});
        }
        {
            var Q0;
            Q0=makeQuery(id+"F57.opExtrude","SWEPT_FACE",FACE,{"disambiguationData":[OSD([sQuery(id+"F56.wireOp",EDGE,"E68.8")])]});
            var sketch = newSketch(context, id + "F84", { "sketchPlane" : qUnion([Q0])});
            skFitSpline(sketch, "E88", {"points": [v(93.92, 18.07) * mm, v(91.19, 17.42) * mm, v(86.3, 18) * mm, v(89.1, 17.63) * mm, v(90.92, 17.57) * mm, v(91.57, 17.81) * mm, v(93.92, 18.07) * mm]});
            skSolve(sketch);
        }
        {
            var Q0;
            {var subQ0=sQuery(id+"F84.wireOp",EDGE,"E88");var subQ1=sQuery(id+"F56.wireOp",EDGE,"E68.8");var subQ2=makeQuery(id+"F61.boolean.opBoolean","MERGE",EDGE,{"derivedFrom":[makeQuery(id+"F57.opExtrude","CAP_EDGE",EDGE,{"disambiguationData":[OSD([subQ1])],"isStart":true}),makeQuery(id+"F61.opExtrude","CAP_EDGE",EDGE,{"disambiguationData":[OSD([subQ1])],"isStart":true})]});var subQ3=makeQuery(id+"F84.imprint","INTERSECT",VERTEX,{"disambiguationData":[OD(0.0)],"derivedFrom":[subQ2,subQ0]});Q0=makeQuery(id+"F84.imprint","IMPRINT",FACE,{"disambiguationData":[TD([[makeQuery(id+"F84.imprint","IMPRINT",EDGE,{"disambiguationData":[TD([[subQ3,1.0]])],"derivedFrom":subQ0}),-1.0]])]});}
            extrude(context, id + "F85", {"entities" : qUnion([Q0]), "operationType" : NewBodyOperationType.ADD, "depth" : 2.8 * mm, "offsetDistance" : 25.4 * mm});
        }
        {
            var Q0;
            Q0=makeQuery(id+"F57.opExtrude","SWEPT_FACE",FACE,{"disambiguationData":[OSD([sQuery(id+"F56.wireOp",EDGE,"E68.9")])]});
            var sketch = newSketch(context, id + "F86", { "sketchPlane" : qUnion([Q0])});
            skFitSpline(sketch, "E89", {"points": [v(93.98, 18.5) * mm, v(91.27, 17.75) * mm, v(86.36, 18.15) * mm, v(89.19, 17.88) * mm, v(91, 17.89) * mm, v(91.64, 18.15) * mm, v(93.98, 18.5) * mm]});
            skSolve(sketch);
        }
        {
            var Q0;
            {var subQ0=sQuery(id+"F86.wireOp",EDGE,"E89");var subQ1=sQuery(id+"F56.wireOp",EDGE,"E68.9");var subQ5=makeQuery(id+"F65.boolean.opBoolean","MERGE",EDGE,{"derivedFrom":[makeQuery(id+"F57.opExtrude","CAP_EDGE",EDGE,{"disambiguationData":[OSD([subQ1])],"isStart":false}),makeQuery(id+"F65.opExtrude","CAP_EDGE",EDGE,{"disambiguationData":[OSD([subQ1])],"isStart":true})]});var subQ9=makeQuery(id+"F86.imprint","INTERSECT",VERTEX,{"derivedFrom":[subQ5,subQ0]});Q0=makeQuery(id+"F86.imprint","IMPRINT",FACE,{"disambiguationData":[TD([[makeQuery(id+"F86.imprint","IMPRINT",EDGE,{"disambiguationData":[TD([[subQ9,-1.0]])],"derivedFrom":subQ0}),-1.0]])]});}
            extrude(context, id + "F87", {"entities" : qUnion([Q0]), "operationType" : NewBodyOperationType.ADD, "depth" : 2.8 * mm, "offsetDistance" : 25.4 * mm});
        }
        {
            var Q0;
            Q0=makeQuery(id+"F57.opExtrude","SWEPT_FACE",FACE,{"disambiguationData":[OSD([sQuery(id+"F56.wireOp",EDGE,"E68.10")])]});
            var sketch = newSketch(context, id + "F88", { "sketchPlane" : qUnion([Q0])});
            skFitSpline(sketch, "E90", {"points": [v(14.72, -93.98) * mm, v(13.97, -91.27) * mm, v(14.38, -86.36) * mm, v(14.1, -89.19) * mm, v(14.1, -91) * mm, v(14.38, -91.64) * mm, v(14.72, -93.98) * mm]});
            skSolve(sketch);
        }
        {
            var Q0;
            {var subQ0=sQuery(id+"F88.wireOp",EDGE,"E90");var subQ1=sQuery(id+"F56.wireOp",EDGE,"E68.10");var subQ2=makeQuery(id+"F65.boolean.opBoolean","MERGE",EDGE,{"derivedFrom":[makeQuery(id+"F57.opExtrude","CAP_EDGE",EDGE,{"disambiguationData":[OSD([subQ1])],"isStart":false}),makeQuery(id+"F65.opExtrude","CAP_EDGE",EDGE,{"disambiguationData":[OSD([subQ1])],"isStart":true})]});var subQ9=makeQuery(id+"F88.imprint","INTERSECT",VERTEX,{"derivedFrom":[subQ2,subQ0]});Q0=makeQuery(id+"F88.imprint","IMPRINT",FACE,{"disambiguationData":[TD([[makeQuery(id+"F88.imprint","IMPRINT",EDGE,{"disambiguationData":[TD([[subQ9,-1.0]])],"derivedFrom":subQ0}),-1.0]])]});}
            extrude(context, id + "F89", {"entities" : qUnion([Q0]), "operationType" : NewBodyOperationType.ADD, "depth" : 2.8 * mm, "offsetDistance" : 25.4 * mm});
        }
        {
            var Q0;
            Q0=makeQuery(id+"F57.opExtrude","SWEPT_FACE",FACE,{"disambiguationData":[OSD([sQuery(id+"F56.wireOp",EDGE,"E68.11")])]});
            var sketch = newSketch(context, id + "F90", { "sketchPlane" : qUnion([Q0])});
            skFitSpline(sketch, "E91", {"points": [v(7.66, -93.98) * mm, v(6.92, -91.27) * mm, v(7.32, -86.36) * mm, v(7.04, -89.19) * mm, v(7.05, -91) * mm, v(7.32, -91.64) * mm, v(7.66, -93.98) * mm]});
            skSolve(sketch);
        }
        {
            var Q0;
            {var subQ0=sQuery(id+"F90.wireOp",EDGE,"E91");var subQ1=sQuery(id+"F56.wireOp",EDGE,"E68.11");var subQ6=makeQuery(id+"F65.boolean.opBoolean","MERGE",EDGE,{"derivedFrom":[makeQuery(id+"F57.opExtrude","CAP_EDGE",EDGE,{"disambiguationData":[OSD([subQ1])],"isStart":false}),makeQuery(id+"F65.opExtrude","CAP_EDGE",EDGE,{"disambiguationData":[OSD([subQ1])],"isStart":true})]});var subQ8=makeQuery(id+"F90.imprint","INTERSECT",VERTEX,{"derivedFrom":[subQ6,subQ0]});Q0=makeQuery(id+"F90.imprint","IMPRINT",FACE,{"disambiguationData":[TD([[makeQuery(id+"F90.imprint","IMPRINT",EDGE,{"disambiguationData":[TD([[subQ8,-1.0]])],"derivedFrom":subQ0}),-1.0]])]});}
            extrude(context, id + "F91", {"entities" : qUnion([Q0]), "operationType" : NewBodyOperationType.ADD, "depth" : 2.8 * mm, "offsetDistance" : 25.4 * mm});
        }
        {
            var Q0;
            Q0=makeQuery(id+"F57.opExtrude","SWEPT_FACE",FACE,{"disambiguationData":[OSD([sQuery(id+"F56.wireOp",EDGE,"E67.12")])]});
            var sketch = newSketch(context, id + "F92", { "sketchPlane" : qUnion([Q0])});
            skFitSpline(sketch, "E92", {"points": [v(-9.55, -93.98) * mm, v(-10.18, -91.24) * mm, v(-9.57, -86.35) * mm, v(-9.96, -89.17) * mm, v(-10.03, -90.98) * mm, v(-9.79, -91.62) * mm, v(-9.55, -93.98) * mm]});
            skSolve(sketch);
        }
        {
            var Q0;
            {var subQ0=sQuery(id+"F92.wireOp",EDGE,"E92");var subQ1=sQuery(id+"F56.wireOp",EDGE,"E67.12");var subQ5=makeQuery(id+"F63.boolean.opBoolean","MERGE",EDGE,{"derivedFrom":[makeQuery(id+"F57.opExtrude","CAP_EDGE",EDGE,{"disambiguationData":[OSD([subQ1])],"isStart":false}),makeQuery(id+"F63.opExtrude","CAP_EDGE",EDGE,{"disambiguationData":[OSD([subQ1])],"isStart":true})]});var subQ9=makeQuery(id+"F92.imprint","INTERSECT",VERTEX,{"derivedFrom":[subQ5,subQ0]});Q0=makeQuery(id+"F92.imprint","IMPRINT",FACE,{"disambiguationData":[TD([[makeQuery(id+"F92.imprint","IMPRINT",EDGE,{"disambiguationData":[TD([[subQ9,-1.0]])],"derivedFrom":subQ0}),-1.0]])]});}
            extrude(context, id + "F93", {"entities" : qUnion([Q0]), "operationType" : NewBodyOperationType.ADD, "depth" : 2.8 * mm, "offsetDistance" : 25.4 * mm});
        }
        {
            var Q0;
            Q0=makeQuery(id+"F57.opExtrude","SWEPT_FACE",FACE,{"disambiguationData":[OSD([sQuery(id+"F56.wireOp",EDGE,"E67.0")])]});
            var sketch = newSketch(context, id + "F94", { "sketchPlane" : qUnion([Q0])});
            skFitSpline(sketch, "E93", {"points": [v(-15.65, -93.98) * mm, v(-16.4, -91.27) * mm, v(-16, -86.36) * mm, v(-16.27, -89.19) * mm, v(-16.26, -91) * mm, v(-16, -91.64) * mm, v(-15.65, -93.98) * mm]});
            skSolve(sketch);
        }
        {
            var Q0;
            {var subQ0=sQuery(id+"F94.wireOp",EDGE,"E93");var subQ1=sQuery(id+"F56.wireOp",EDGE,"E67.0");var subQ2=makeQuery(id+"F63.boolean.opBoolean","MERGE",EDGE,{"derivedFrom":[makeQuery(id+"F57.opExtrude","CAP_EDGE",EDGE,{"disambiguationData":[OSD([subQ1])],"isStart":false}),makeQuery(id+"F63.opExtrude","CAP_EDGE",EDGE,{"disambiguationData":[OSD([subQ1])],"isStart":true})]});var subQ9=makeQuery(id+"F94.imprint","INTERSECT",VERTEX,{"derivedFrom":[subQ2,subQ0]});Q0=makeQuery(id+"F94.imprint","IMPRINT",FACE,{"disambiguationData":[TD([[makeQuery(id+"F94.imprint","IMPRINT",EDGE,{"disambiguationData":[TD([[subQ9,-1.0]])],"derivedFrom":subQ0}),-1.0]])]});}
            extrude(context, id + "F95", {"entities" : qUnion([Q0]), "operationType" : NewBodyOperationType.ADD, "depth" : 2.8 * mm, "offsetDistance" : 25.4 * mm});
        }
        {
            var Q0;
            Q0=makeQuery(id+"F57.opExtrude","SWEPT_FACE",FACE,{"disambiguationData":[OSD([sQuery(id+"F56.wireOp",EDGE,"E67.1")])]});
            var sketch = newSketch(context, id + "F96", { "sketchPlane" : qUnion([Q0])});
            skFitSpline(sketch, "E94", {"points": [v(-93.96, 18.1) * mm, v(-91.22, 18.72) * mm, v(-86.34, 18.08) * mm, v(-89.15, 18.5) * mm, v(-90.96, 18.57) * mm, v(-91.6, 18.33) * mm, v(-93.96, 18.1) * mm]});
            skSolve(sketch);
        }
        {
            var Q0;
            {var subQ0=sQuery(id+"F56.wireOp",EDGE,"E67.1");var subQ4=sQuery(id+"F96.wireOp",EDGE,"E94");var subQ6=makeQuery(id+"F63.boolean.opBoolean","MERGE",EDGE,{"derivedFrom":[makeQuery(id+"F57.opExtrude","CAP_EDGE",EDGE,{"disambiguationData":[OSD([subQ0])],"isStart":false}),makeQuery(id+"F63.opExtrude","CAP_EDGE",EDGE,{"disambiguationData":[OSD([subQ0])],"isStart":true})]});var subQ9=makeQuery(id+"F96.imprint","INTERSECT",VERTEX,{"disambiguationData":[OD(0.0)],"derivedFrom":[subQ6,subQ4]});Q0=makeQuery(id+"F96.imprint","IMPRINT",FACE,{"disambiguationData":[TD([[makeQuery(id+"F96.imprint","IMPRINT",EDGE,{"disambiguationData":[TD([[subQ9,-1.0]])],"derivedFrom":subQ4}),-1.0]])]});}
            extrude(context, id + "F97", {"entities" : qUnion([Q0]), "operationType" : NewBodyOperationType.ADD, "depth" : 2.8 * mm, "offsetDistance" : 25.4 * mm});
        }
        {
            var Q0;
            Q0=makeQuery(id+"F57.opExtrude","SWEPT_FACE",FACE,{"disambiguationData":[OSD([sQuery(id+"F56.wireOp",EDGE,"E67.2")])]});
            var sketch = newSketch(context, id + "F98", { "sketchPlane" : qUnion([Q0])});
            skFitSpline(sketch, "E95", {"points": [v(-93.98, 16.28) * mm, v(-91.27, 17.02) * mm, v(-86.36, 16.62) * mm, v(-89.19, 16.9) * mm, v(-91, 16.88) * mm, v(-91.64, 16.62) * mm, v(-93.98, 16.28) * mm]});
            skSolve(sketch);
        }
        {
            var Q0;
            {var subQ0=sQuery(id+"F98.wireOp",EDGE,"E95");var subQ1=sQuery(id+"F56.wireOp",EDGE,"E67.2");var subQ2=makeQuery(id+"F63.boolean.opBoolean","MERGE",EDGE,{"derivedFrom":[makeQuery(id+"F57.opExtrude","CAP_EDGE",EDGE,{"disambiguationData":[OSD([subQ1])],"isStart":false}),makeQuery(id+"F63.opExtrude","CAP_EDGE",EDGE,{"disambiguationData":[OSD([subQ1])],"isStart":true})]});var subQ9=makeQuery(id+"F98.imprint","INTERSECT",VERTEX,{"derivedFrom":[subQ2,subQ0]});Q0=makeQuery(id+"F98.imprint","IMPRINT",FACE,{"disambiguationData":[TD([[makeQuery(id+"F98.imprint","IMPRINT",EDGE,{"disambiguationData":[TD([[subQ9,-1.0]])],"derivedFrom":subQ0}),-1.0]])]});}
            extrude(context, id + "F99", {"entities" : qUnion([Q0]), "operationType" : NewBodyOperationType.ADD, "depth" : 2.8 * mm, "offsetDistance" : 25.4 * mm});
        }
        {
            var Q0;
            Q0=makeQuery(id+"F57.opExtrude","SWEPT_FACE",FACE,{"disambiguationData":[OSD([sQuery(id+"F56.wireOp",EDGE,"E67.3")])]});
            var sketch = newSketch(context, id + "F100", { "sketchPlane" : qUnion([Q0])});
            skFitSpline(sketch, "E96", {"points": [v(-93.98, 10.65) * mm, v(-91.24, 11.28) * mm, v(-86.35, 10.66) * mm, v(-89.17, 11.06) * mm, v(-90.98, 11.13) * mm, v(-91.62, 10.89) * mm, v(-93.98, 10.65) * mm]});
            skSolve(sketch);
        }
        {
            var Q0;
            {var subQ0=sQuery(id+"F100.wireOp",EDGE,"E96");var subQ1=sQuery(id+"F56.wireOp",EDGE,"E67.3");var subQ2=makeQuery(id+"F59.boolean.opBoolean","SPLIT",EDGE,{"derivedFrom":makeQuery(id+"F57.opExtrude","CAP_EDGE",EDGE,{"disambiguationData":[OSD([subQ1])],"isStart":true})});var subQ3=makeQuery(id+"F100.imprint","INTERSECT",VERTEX,{"disambiguationData":[OD(0.0)],"derivedFrom":[subQ2,subQ0]});Q0=makeQuery(id+"F100.imprint","IMPRINT",FACE,{"disambiguationData":[TD([[makeQuery(id+"F100.imprint","IMPRINT",EDGE,{"disambiguationData":[TD([[subQ3,-1.0]])],"derivedFrom":subQ2}),-1.0]])]});}
            extrude(context, id + "F101", {"entities" : qUnion([Q0]), "operationType" : NewBodyOperationType.ADD, "depth" : 2.8 * mm, "offsetDistance" : 25.4 * mm});
        }
        {
            var Q0;
            Q0=makeQuery(id+"F57.opExtrude","SWEPT_FACE",FACE,{"disambiguationData":[OSD([sQuery(id+"F56.wireOp",EDGE,"E67.4")])]});
            var sketch = newSketch(context, id + "F102", { "sketchPlane" : qUnion([Q0])});
            skFitSpline(sketch, "E97", {"points": [v(2.49, 93.98) * mm, v(3.23, 91.27) * mm, v(2.83, 86.36) * mm, v(3.1, 89.19) * mm, v(3.1, 91) * mm, v(2.83, 91.64) * mm, v(2.49, 93.98) * mm]});
            skSolve(sketch);
        }
        {
            var Q0;
            {var subQ0=sQuery(id+"F102.wireOp",EDGE,"E97");var subQ1=sQuery(id+"F56.wireOp",EDGE,"E67.4");var subQ2=makeQuery(id+"F63.boolean.opBoolean","MERGE",EDGE,{"derivedFrom":[makeQuery(id+"F57.opExtrude","CAP_EDGE",EDGE,{"disambiguationData":[OSD([subQ1])],"isStart":false}),makeQuery(id+"F63.opExtrude","CAP_EDGE",EDGE,{"disambiguationData":[OSD([subQ1])],"isStart":true})]});var subQ9=makeQuery(id+"F102.imprint","INTERSECT",VERTEX,{"derivedFrom":[subQ2,subQ0]});Q0=makeQuery(id+"F102.imprint","IMPRINT",FACE,{"disambiguationData":[TD([[makeQuery(id+"F102.imprint","IMPRINT",EDGE,{"disambiguationData":[TD([[subQ9,-1.0]])],"derivedFrom":subQ0}),-1.0]])]});}
            extrude(context, id + "F103", {"entities" : qUnion([Q0]), "operationType" : NewBodyOperationType.ADD, "depth" : 2.8 * mm, "offsetDistance" : 25.4 * mm});
        }
        {
            var Q0;
            Q0=makeQuery(id+"F57.opExtrude","SWEPT_FACE",FACE,{"disambiguationData":[OSD([sQuery(id+"F56.wireOp",EDGE,"E67.5")])]});
            var sketch = newSketch(context, id + "F104", { "sketchPlane" : qUnion([Q0])});
            skFitSpline(sketch, "E98", {"points": [v(-6.26, 93.98) * mm, v(-5.62, 91.25) * mm, v(-6.22, 86.35) * mm, v(-5.83, 89.17) * mm, v(-5.77, 90.98) * mm, v(-6.01, 91.63) * mm, v(-6.26, 93.98) * mm]});
            skSolve(sketch);
        }
        {
            var Q0;
            {var subQ0=sQuery(id+"F104.wireOp",EDGE,"E98");var subQ1=sQuery(id+"F56.wireOp",EDGE,"E67.5");var subQ2=makeQuery(id+"F63.boolean.opBoolean","MERGE",EDGE,{"derivedFrom":[makeQuery(id+"F57.opExtrude","CAP_EDGE",EDGE,{"disambiguationData":[OSD([subQ1])],"isStart":false}),makeQuery(id+"F63.opExtrude","CAP_EDGE",EDGE,{"disambiguationData":[OSD([subQ1])],"isStart":true})]});var subQ3=makeQuery(id+"F104.imprint","INTERSECT",VERTEX,{"disambiguationData":[OD(0.0)],"derivedFrom":[subQ2,subQ0]});Q0=makeQuery(id+"F104.imprint","IMPRINT",FACE,{"disambiguationData":[TD([[makeQuery(id+"F104.imprint","IMPRINT",EDGE,{"disambiguationData":[TD([[subQ3,-1.0]])],"derivedFrom":subQ2}),1.0]])]});}
            extrude(context, id + "F105", {"entities" : qUnion([Q0]), "operationType" : NewBodyOperationType.ADD, "depth" : 2.8 * mm, "offsetDistance" : 25.4 * mm});
        }
        {
            var Q0;
            Q0=makeQuery(id+"F57.opExtrude","SWEPT_FACE",FACE,{"disambiguationData":[OSD([sQuery(id+"F56.wireOp",EDGE,"E67.6")])]});
            var sketch = newSketch(context, id + "F106", { "sketchPlane" : qUnion([Q0])});
            skFitSpline(sketch, "E99", {"points": [v(-13.8, 93.98) * mm, v(-13.06, 91.27) * mm, v(-13.46, 86.36) * mm, v(-13.18, 89.19) * mm, v(-13.2, 91) * mm, v(-13.46, 91.64) * mm, v(-13.8, 93.98) * mm]});
            skSolve(sketch);
        }
        {
            var Q0;
            {var subQ0=sQuery(id+"F106.wireOp",EDGE,"E99");var subQ1=sQuery(id+"F56.wireOp",EDGE,"E67.6");var subQ3=sQuery(id+"F56.wireOp",EDGE,"E67.7");var subQ4=makeQuery(id+"F57.opExtrude","SWEPT_EDGE",EDGE,{"disambiguationData":[OSD([subQ1,subQ3])]});var subQ6=makeQuery(id+"F106.imprint","INTERSECT",VERTEX,{"derivedFrom":[subQ4,subQ0]});Q0=makeQuery(id+"F106.imprint","IMPRINT",FACE,{"disambiguationData":[TD([[makeQuery(id+"F106.imprint","IMPRINT",EDGE,{"disambiguationData":[TD([[subQ6,1.0]])],"derivedFrom":subQ4}),1.0]])]});}
            extrude(context, id + "F107", {"entities" : qUnion([Q0]), "operationType" : NewBodyOperationType.ADD, "depth" : 2.8 * mm, "offsetDistance" : 25.4 * mm});
        }
        {
            var Q0;
            Q0=makeQuery(id+"F57.opExtrude","SWEPT_FACE",FACE,{"disambiguationData":[OSD([sQuery(id+"F56.wireOp",EDGE,"E67.7")])]});
            var sketch = newSketch(context, id + "F108", { "sketchPlane" : qUnion([Q0])});
            skFitSpline(sketch, "E100", {"points": [v(93.98, 18.2) * mm, v(91.24, 17.57) * mm, v(86.35, 18.2) * mm, v(89.16, 17.8) * mm, v(90.98, 17.72) * mm, v(91.62, 17.96) * mm, v(93.98, 18.2) * mm]});
            skSolve(sketch);
        }
        {
            var Q0;
            {var subQ0=sQuery(id+"F108.wireOp",EDGE,"E100");var subQ1=sQuery(id+"F56.wireOp",EDGE,"E67.7");var subQ6=makeQuery(id+"F57.opExtrude","CAP_EDGE",EDGE,{"disambiguationData":[OSD([subQ1])],"isStart":true});var subQ8=makeQuery(id+"F108.imprint","INTERSECT",VERTEX,{"disambiguationData":[OD(0.0)],"derivedFrom":[subQ6,subQ0]});Q0=makeQuery(id+"F108.imprint","IMPRINT",FACE,{"disambiguationData":[TD([[makeQuery(id+"F108.imprint","IMPRINT",EDGE,{"disambiguationData":[TD([[subQ8,-1.0]])],"derivedFrom":subQ6}),-1.0]])]});}
            extrude(context, id + "F109", {"entities" : qUnion([Q0]), "operationType" : NewBodyOperationType.ADD, "depth" : 2.8 * mm, "offsetDistance" : 25.4 * mm});
        }
        {
            var Q0;
            Q0=makeQuery(id+"F57.opExtrude","SWEPT_FACE",FACE,{"disambiguationData":[OSD([sQuery(id+"F56.wireOp",EDGE,"E67.8")])]});
            var sketch = newSketch(context, id + "F110", { "sketchPlane" : qUnion([Q0])});
            skFitSpline(sketch, "E101", {"points": [v(93.98, 18.52) * mm, v(91.24, 17.89) * mm, v(86.35, 18.5) * mm, v(89.17, 18.1) * mm, v(90.98, 18.04) * mm, v(91.62, 18.28) * mm, v(93.98, 18.52) * mm]});
            skSolve(sketch);
        }
        {
            var Q0;
            {var subQ0=sQuery(id+"F110.wireOp",EDGE,"E101");var subQ1=sQuery(id+"F56.wireOp",EDGE,"E67.9");var subQ2=sQuery(id+"F56.wireOp",EDGE,"E67.8");var subQ10=makeQuery(id+"F57.opExtrude","SWEPT_EDGE",EDGE,{"disambiguationData":[OSD([subQ2,subQ1])]});var subQ12=makeQuery(id+"F110.imprint","INTERSECT",VERTEX,{"derivedFrom":[subQ10,subQ0]});Q0=makeQuery(id+"F110.imprint","IMPRINT",FACE,{"disambiguationData":[TD([[makeQuery(id+"F110.imprint","IMPRINT",EDGE,{"disambiguationData":[TD([[subQ12,1.0]])],"derivedFrom":subQ10}),1.0]])]});}
            extrude(context, id + "F111", {"entities" : qUnion([Q0]), "operationType" : NewBodyOperationType.ADD, "depth" : 2.8 * mm, "offsetDistance" : 25.4 * mm});
        }
        {
            var Q0;
            Q0=makeQuery(id+"F57.opExtrude","SWEPT_FACE",FACE,{"disambiguationData":[OSD([sQuery(id+"F56.wireOp",EDGE,"E67.9")])]});
            var sketch = newSketch(context, id + "F112", { "sketchPlane" : qUnion([Q0])});
            skFitSpline(sketch, "E102", {"points": [v(94, 14.63) * mm, v(91.3, 13.88) * mm, v(86.39, 14.28) * mm, v(89.21, 14) * mm, v(91.03, 14.02) * mm, v(91.66, 14.28) * mm, v(94, 14.63) * mm]});
            skSolve(sketch);
        }
        {
            var Q0;
            {var subQ0=sQuery(id+"F112.wireOp",EDGE,"E102");var subQ1=sQuery(id+"F56.wireOp",EDGE,"E67.9");var subQ2=makeQuery(id+"F111.boolean.opBoolean","SPLIT",EDGE,{"derivedFrom":makeQuery(id+"F57.opExtrude","SWEPT_EDGE",EDGE,{"disambiguationData":[OSD([sQuery(id+"F56.wireOp",EDGE,"E67.8"),subQ1])]})});var subQ3=makeQuery(id+"F112.imprint","INTERSECT",VERTEX,{"disambiguationData":[OD(0.0)],"derivedFrom":[subQ2,subQ0]});Q0=makeQuery(id+"F112.imprint","IMPRINT",FACE,{"disambiguationData":[TD([[makeQuery(id+"F112.imprint","IMPRINT",EDGE,{"disambiguationData":[TD([[subQ3,1.0]])],"derivedFrom":subQ0}),-1.0]])]});}
            extrude(context, id + "F113", {"entities" : qUnion([Q0]), "operationType" : NewBodyOperationType.ADD, "depth" : 2.8 * mm, "offsetDistance" : 25.4 * mm});
        }
        {
            var Q0;
            Q0=makeQuery(id+"F57.opExtrude","SWEPT_FACE",FACE,{"disambiguationData":[OSD([sQuery(id+"F56.wireOp",EDGE,"E67.10")])]});
            var sketch = newSketch(context, id + "F114", { "sketchPlane" : qUnion([Q0])});
            skFitSpline(sketch, "E103", {"points": [v(7.56, -94) * mm, v(6.95, -91.26) * mm, v(7.6, -86.37) * mm, v(7.18, -89.18) * mm, v(7.1, -91) * mm, v(7.34, -91.64) * mm, v(7.56, -94) * mm]});
            skSolve(sketch);
        }
        {
            var Q0;
            {var subQ0=sQuery(id+"F114.wireOp",EDGE,"E103");var subQ1=sQuery(id+"F56.wireOp",EDGE,"E67.10");var subQ2=makeQuery(id+"F57.opExtrude","SWEPT_EDGE",EDGE,{"disambiguationData":[OSD([subQ1,sQuery(id+"F56.wireOp",EDGE,"E67.11")])]});var subQ9=makeQuery(id+"F114.imprint","INTERSECT",VERTEX,{"disambiguationData":[OD(0.0)],"derivedFrom":[subQ2,subQ0]});Q0=makeQuery(id+"F114.imprint","IMPRINT",FACE,{"disambiguationData":[TD([[makeQuery(id+"F114.imprint","IMPRINT",EDGE,{"disambiguationData":[TD([[subQ9,1.0]])],"derivedFrom":subQ0}),-1.0]])]});}
            extrude(context, id + "F115", {"entities" : qUnion([Q0]), "operationType" : NewBodyOperationType.ADD, "depth" : 2.8 * mm, "offsetDistance" : 25.4 * mm});
        }
        {
            var Q0;
            Q0=makeQuery(id+"F57.opExtrude","SWEPT_FACE",FACE,{"disambiguationData":[OSD([sQuery(id+"F56.wireOp",EDGE,"E67.11")])]});
            var sketch = newSketch(context, id + "F116", { "sketchPlane" : qUnion([Q0])});
            skFitSpline(sketch, "E104", {"points": [v(-1.16, -93.98) * mm, v(-1.9, -91.27) * mm, v(-1.5, -86.36) * mm, v(-1.78, -89.19) * mm, v(-1.77, -91) * mm, v(-1.5, -91.64) * mm, v(-1.16, -93.98) * mm]});
            skSolve(sketch);
        }
        {
            var Q0;
            {var subQ0=sQuery(id+"F116.wireOp",EDGE,"E104");var subQ1=sQuery(id+"F56.wireOp",EDGE,"E67.11");var subQ5=makeQuery(id+"F63.boolean.opBoolean","MERGE",EDGE,{"derivedFrom":[makeQuery(id+"F57.opExtrude","CAP_EDGE",EDGE,{"disambiguationData":[OSD([subQ1])],"isStart":false}),makeQuery(id+"F63.opExtrude","CAP_EDGE",EDGE,{"disambiguationData":[OSD([subQ1])],"isStart":true})]});var subQ9=makeQuery(id+"F116.imprint","INTERSECT",VERTEX,{"derivedFrom":[subQ5,subQ0]});Q0=makeQuery(id+"F116.imprint","IMPRINT",FACE,{"disambiguationData":[TD([[makeQuery(id+"F116.imprint","IMPRINT",EDGE,{"disambiguationData":[TD([[subQ9,-1.0]])],"derivedFrom":subQ0}),-1.0]])]});}
            extrude(context, id + "F117", {"entities" : qUnion([Q0]), "operationType" : NewBodyOperationType.ADD, "depth" : 2.8 * mm, "offsetDistance" : 25.4 * mm});
        }
    });
